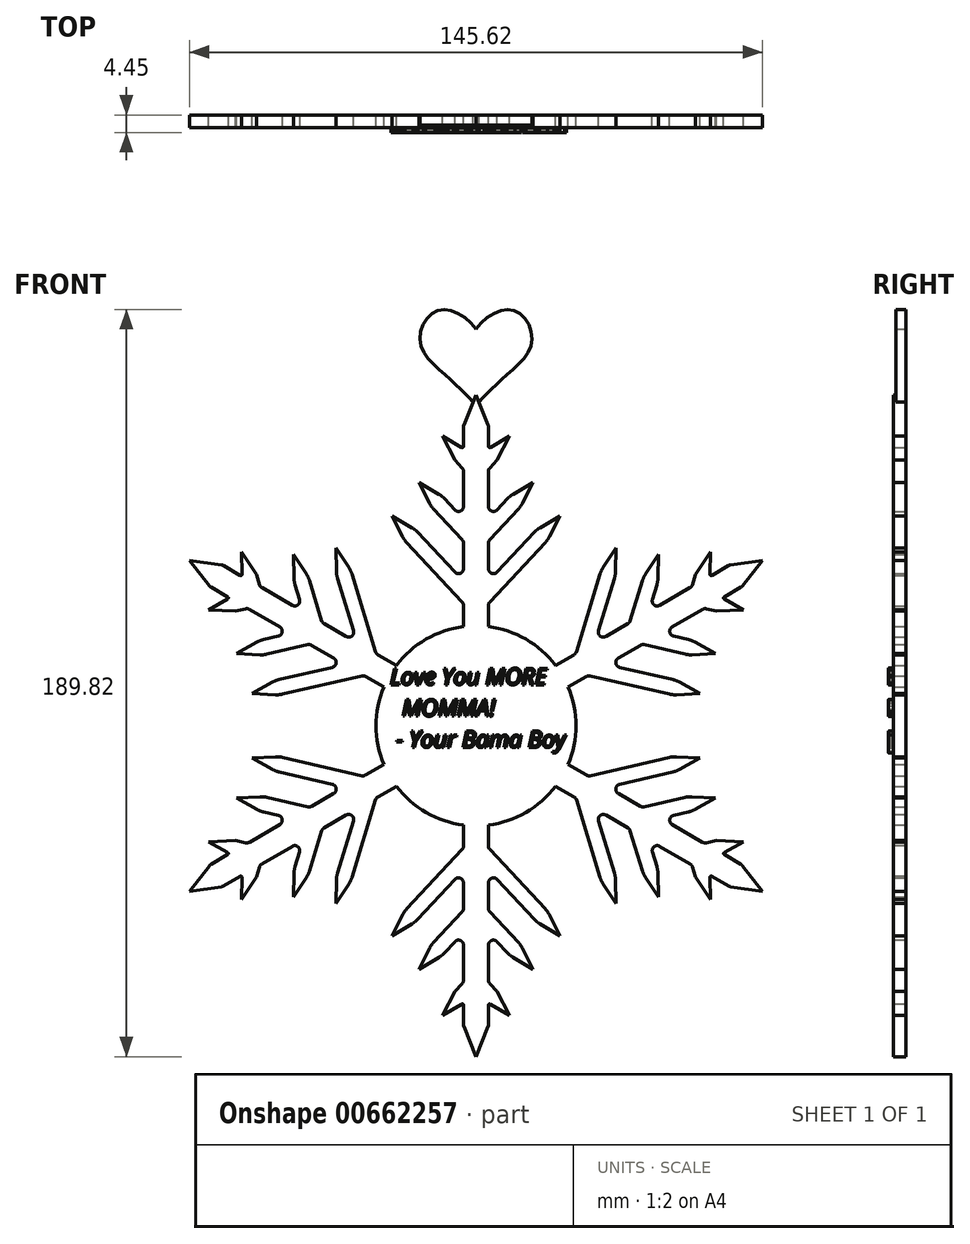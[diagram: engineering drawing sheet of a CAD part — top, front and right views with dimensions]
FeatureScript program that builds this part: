
annotation { "Feature Type Name" : "Feature", "Feature Type Description" : "" }
export const myFeature = defineFeature(function(context is Context, id is Id, definition is map)
    precondition{}
    {
        {
            var Q0;
            Q0=qCreatedBy(makeId("Front.planeOp"),FACE);
            var sketch = newSketch(context, id + "F0", { "sketchPlane" : qUnion([Q0])});
            skLineSegment(sketch, "E0", {"start": v(0, 76.2) * mm, "end": v(0, -76.2) * mm, "construction": true});
            skLineSegment(sketch, "E1", {"start": v(-76.2, 0) * mm, "end": v(76.2, 0) * mm, "construction": true});
            skPoint(sketch, "E2", {"position": v(0, 0) * mm});
            skArc(sketch, "E3", {"start": v(-23.41, 9.85) * mm, "mid": v(-25.4, 0) * mm, "end": v(-23.41, -9.85) * mm});
            skLineSegment(sketch, "E4.left", {"start": v(-3.17, 75.95) * mm, "end": v(-3.17, 71) * mm});
            skLineSegment(sketch, "E4.right", {"start": v(3.17, 75.95) * mm, "end": v(3.17, 71) * mm});
            skLineSegment(sketch, "E5", {"start": v(-3.17, 33.88) * mm, "end": v(-21.33, 53.35) * mm});
            skLineSegment(sketch, "E6", {"start": v(-3.17, 49.7) * mm, "end": v(-14.52, 61.87) * mm});
            skLineSegment(sketch, "E7", {"start": v(-3.17, 67.95) * mm, "end": v(-8.46, 73.61) * mm});
            skLineSegment(sketch, "E8", {"start": v(-3.52, 31.46) * mm, "end": v(-17.62, 46.58) * mm});
            skLineSegment(sketch, "E9", {"start": v(-14.83, 49.18) * mm, "end": v(-5.37, 39.03) * mm});
            skLineSegment(sketch, "E10", {"start": v(-3.52, 47.28) * mm, "end": v(-10.8, 55.1) * mm});
            skLineSegment(sketch, "E11", {"start": v(-8.02, 57.7) * mm, "end": v(-5.37, 54.85) * mm});
            skLineSegment(sketch, "E12", {"start": v(-3.52, 65.52) * mm, "end": v(-5.36, 67.5) * mm});
            skLineSegment(sketch, "E13", {"start": v(-18.64, 48.04) * mm, "end": v(-21.33, 53.35) * mm});
            skLineSegment(sketch, "E14", {"start": v(-16.22, 50.3) * mm, "end": v(-21.33, 53.35) * mm});
            skLineSegment(sketch, "E15", {"start": v(-3.64, 70.73) * mm, "end": v(-8.46, 73.61) * mm});
            skLineSegment(sketch, "E16", {"start": v(-5.36, 67.5) * mm, "end": v(-8.46, 73.61) * mm});
            skLineSegment(sketch, "E17", {"start": v(-11.83, 56.56) * mm, "end": v(-14.52, 61.87) * mm});
            skLineSegment(sketch, "E18", {"start": v(-9.4, 58.81) * mm, "end": v(-14.52, 61.87) * mm});
            skPoint(sketch, "E19.orphan", {"position": v(-7.07, 74.91) * mm});
            skPoint(sketch, "E20.orphan", {"position": v(-9.85, 72.31) * mm});
            skPoint(sketch, "E21.orphan", {"position": v(-13.12, 63.17) * mm});
            skPoint(sketch, "E22.orphan", {"position": v(-15.91, 60.57) * mm});
            skPoint(sketch, "E23.orphan", {"position": v(-19.94, 54.65) * mm});
            skPoint(sketch, "E24.orphan", {"position": v(-22.72, 52.05) * mm});
            skPoint(sketch, "E25.visualSharp", {"position": v(-15.45, 49.84) * mm});
            skArc(sketch, "E25.filletArc", {"start": v(-14.83, 49.18) * mm, "mid": v(-15.49, 49.79) * mm, "end": v(-16.22, 50.3) * mm});
            skPoint(sketch, "E26.visualSharp", {"position": v(-18.23, 47.24) * mm});
            skArc(sketch, "E26.filletArc", {"start": v(-18.64, 48.04) * mm, "mid": v(-18.18, 47.28) * mm, "end": v(-17.62, 46.58) * mm});
            skPoint(sketch, "E27.visualSharp", {"position": v(-11.42, 55.75) * mm});
            skArc(sketch, "E27.filletArc", {"start": v(-11.83, 56.56) * mm, "mid": v(-11.37, 55.79) * mm, "end": v(-10.8, 55.1) * mm});
            skPoint(sketch, "E28.visualSharp", {"position": v(-8.63, 58.35) * mm});
            skArc(sketch, "E28.filletArc", {"start": v(-8.02, 57.7) * mm, "mid": v(-8.67, 58.3) * mm, "end": v(-9.4, 58.81) * mm});
            skLineSegment(sketch, "E29.trimOffspring", {"start": v(-3.17, 30.59) * mm, "end": v(-3.17, 25.2) * mm});
            skLineSegment(sketch, "E30.trimOffspring", {"start": v(-3.17, 46.41) * mm, "end": v(-3.17, 39.9) * mm});
            skLineSegment(sketch, "E31.trimOffspring", {"start": v(-3.17, 64.65) * mm, "end": v(-3.17, 55.72) * mm});
            skPoint(sketch, "E32.visualSharp", {"position": v(-3.17, 70.46) * mm});
            skArc(sketch, "E32.filletArc", {"start": v(-3.64, 70.73) * mm, "mid": v(-3.33, 70.73) * mm, "end": v(-3.17, 71) * mm});
            skPoint(sketch, "E33.visualSharp", {"position": v(-3.17, 65.15) * mm});
            skArc(sketch, "E33.filletArc", {"start": v(-3.18, 64.65) * mm, "mid": v(-3.26, 65.12) * mm, "end": v(-3.52, 65.52) * mm});
            skPoint(sketch, "E34.visualSharp", {"position": v(-3.17, 52.5) * mm});
            skArc(sketch, "E34.filletArc", {"start": v(-5.37, 54.85) * mm, "mid": v(-3.98, 54.54) * mm, "end": v(-3.17, 55.72) * mm});
            skPoint(sketch, "E35.visualSharp", {"position": v(-3.17, 46.91) * mm});
            skArc(sketch, "E35.filletArc", {"start": v(-3.17, 46.41) * mm, "mid": v(-3.26, 46.88) * mm, "end": v(-3.52, 47.28) * mm});
            skPoint(sketch, "E36.visualSharp", {"position": v(-3.17, 36.68) * mm});
            skArc(sketch, "E36.filletArc", {"start": v(-5.37, 39.03) * mm, "mid": v(-3.98, 38.72) * mm, "end": v(-3.17, 39.9) * mm});
            skPoint(sketch, "E37.visualSharp", {"position": v(-3.17, 31.09) * mm});
            skArc(sketch, "E37.filletArc", {"start": v(-3.17, 30.59) * mm, "mid": v(-3.26, 31.05) * mm, "end": v(-3.52, 31.46) * mm});
            skLineSegment(sketch, "E38", {"start": v(-3.08, 76.43) * mm, "end": v(0, 84.07) * mm});
            skLineSegment(sketch, "E39", {"start": v(0, 84.07) * mm, "end": v(3.08, 76.43) * mm});
            skPoint(sketch, "E40.visualSharp", {"position": v(-3.17, 76.2) * mm});
            skArc(sketch, "E40.filletArc", {"start": v(-3.08, 76.43) * mm, "mid": v(-3.15, 76.2) * mm, "end": v(-3.17, 75.95) * mm});
            skPoint(sketch, "E41.visualSharp", {"position": v(3.18, 76.2) * mm});
            skArc(sketch, "E41.filletArc", {"start": v(3.17, 75.95) * mm, "mid": v(3.15, 76.2) * mm, "end": v(3.08, 76.43) * mm});
            skArc(sketch, "E42.MirrorCS", {"start": v(3.08, 76.43) * mm, "mid": v(3.15, 76.2) * mm, "end": v(3.17, 75.95) * mm});
            skArc(sketch, "E43.MirrorCS", {"start": v(3.64, 70.73) * mm, "mid": v(3.33, 70.73) * mm, "end": v(3.17, 71) * mm});
            skArc(sketch, "E44.MirrorCS", {"start": v(11.83, 56.56) * mm, "mid": v(11.37, 55.79) * mm, "end": v(10.8, 55.1) * mm});
            skArc(sketch, "E45.MirrorCS", {"start": v(3.17, 30.59) * mm, "mid": v(3.26, 31.05) * mm, "end": v(3.52, 31.46) * mm});
            skArc(sketch, "E46.MirrorCS", {"start": v(3.18, 64.65) * mm, "mid": v(3.26, 65.12) * mm, "end": v(3.52, 65.52) * mm});
            skArc(sketch, "E47.MirrorCS", {"start": v(3.17, 46.41) * mm, "mid": v(3.26, 46.88) * mm, "end": v(3.52, 47.28) * mm});
            skArc(sketch, "E48.MirrorCS", {"start": v(18.64, 48.04) * mm, "mid": v(18.18, 47.28) * mm, "end": v(17.62, 46.58) * mm});
            skArc(sketch, "E49.MirrorCS", {"start": v(8.02, 57.7) * mm, "mid": v(8.67, 58.3) * mm, "end": v(9.4, 58.81) * mm});
            skArc(sketch, "E50.MirrorCS", {"start": v(14.83, 49.18) * mm, "mid": v(15.49, 49.79) * mm, "end": v(16.22, 50.3) * mm});
            skArc(sketch, "E51.MirrorCS", {"start": v(5.37, 39.03) * mm, "mid": v(3.98, 38.72) * mm, "end": v(3.17, 39.9) * mm});
            skLineSegment(sketch, "E52.MirrorCS", {"start": v(3.52, 65.52) * mm, "end": v(5.36, 67.5) * mm});
            skArc(sketch, "E53.MirrorCS", {"start": v(5.37, 54.85) * mm, "mid": v(3.98, 54.54) * mm, "end": v(3.17, 55.72) * mm});
            skPoint(sketch, "E54.MirrorP", {"position": v(3.17, 65.15) * mm});
            skPoint(sketch, "E55.MirrorP", {"position": v(7.07, 74.91) * mm});
            skLineSegment(sketch, "E56.MirrorCS", {"start": v(11.83, 56.56) * mm, "end": v(14.52, 61.87) * mm});
            skLineSegment(sketch, "E57.MirrorCS", {"start": v(18.64, 48.04) * mm, "end": v(21.33, 53.35) * mm});
            skLineSegment(sketch, "E58.MirrorCS", {"start": v(3.17, 46.41) * mm, "end": v(3.17, 39.9) * mm});
            skPoint(sketch, "E59.MirrorP", {"position": v(3.17, 31.09) * mm});
            skPoint(sketch, "E60.MirrorP", {"position": v(18.23, 47.24) * mm});
            skLineSegment(sketch, "E61.MirrorCS", {"start": v(9.4, 58.81) * mm, "end": v(14.52, 61.87) * mm});
            skLineSegment(sketch, "E62.MirrorCS", {"start": v(16.22, 50.3) * mm, "end": v(21.33, 53.35) * mm});
            skPoint(sketch, "E63.MirrorP", {"position": v(22.72, 52.05) * mm});
            skPoint(sketch, "E64.MirrorP", {"position": v(8.63, 58.35) * mm});
            skPoint(sketch, "E65.MirrorP", {"position": v(3.17, 70.46) * mm});
            skPoint(sketch, "E66.MirrorP", {"position": v(3.17, 76.2) * mm});
            skPoint(sketch, "E67.MirrorP", {"position": v(15.91, 60.57) * mm});
            skPoint(sketch, "E68.MirrorP", {"position": v(9.85, 72.31) * mm});
            skLineSegment(sketch, "E69.MirrorCS", {"start": v(3.17, 33.88) * mm, "end": v(21.33, 53.35) * mm});
            skPoint(sketch, "E70.MirrorP", {"position": v(3.17, 52.5) * mm});
            skPoint(sketch, "E71.MirrorP", {"position": v(19.94, 54.65) * mm});
            skLineSegment(sketch, "E72.MirrorCS", {"start": v(3.17, 49.7) * mm, "end": v(14.52, 61.87) * mm});
            skLineSegment(sketch, "E73.MirrorCS", {"start": v(3.17, 67.95) * mm, "end": v(8.46, 73.61) * mm});
            skLineSegment(sketch, "E74.MirrorCS", {"start": v(3.52, 31.46) * mm, "end": v(17.62, 46.58) * mm});
            skPoint(sketch, "E75.MirrorP", {"position": v(11.42, 55.75) * mm});
            skLineSegment(sketch, "E76.MirrorCS", {"start": v(14.83, 49.18) * mm, "end": v(5.37, 39.03) * mm});
            skLineSegment(sketch, "E77.MirrorCS", {"start": v(3.52, 47.28) * mm, "end": v(10.8, 55.1) * mm});
            skPoint(sketch, "E78.MirrorP", {"position": v(13.12, 63.17) * mm});
            skLineSegment(sketch, "E79.MirrorCS", {"start": v(3.17, 64.65) * mm, "end": v(3.17, 55.72) * mm});
            skLineSegment(sketch, "E80.MirrorCS", {"start": v(5.36, 67.5) * mm, "end": v(8.46, 73.61) * mm});
            skLineSegment(sketch, "E81.MirrorCS", {"start": v(3.64, 70.73) * mm, "end": v(8.46, 73.61) * mm});
            skLineSegment(sketch, "E82.MirrorCS", {"start": v(8.02, 57.7) * mm, "end": v(5.37, 54.85) * mm});
            skPoint(sketch, "E83.MirrorP", {"position": v(3.17, 36.68) * mm});
            skPoint(sketch, "E84.MirrorP", {"position": v(15.45, 49.84) * mm});
            skPoint(sketch, "E85.MirrorP", {"position": v(3.17, 46.91) * mm});
            skLineSegment(sketch, "E86.trimOffspring", {"start": v(3.18, 31.09) * mm, "end": v(3.18, 25.2) * mm});
            skLineSegment(sketch, "E87.trimOffspring", {"start": v(3.18, 46.91) * mm, "end": v(3.18, 39.9) * mm});
            skLineSegment(sketch, "E88.trimOffspring", {"start": v(3.17, 65.15) * mm, "end": v(3.17, 55.72) * mm});
            skPoint(sketch, "E89.1.0", {"position": v(-35.44, 38.3) * mm});
            skPoint(sketch, "E89.1.1", {"position": v(-61.34, 43.58) * mm});
            skPoint(sketch, "E89.1.2", {"position": v(-28.51, 12.8) * mm});
            skPoint(sketch, "E89.1.3", {"position": v(-68.4, 31.34) * mm});
            skLineSegment(sketch, "E89.1.4", {"start": v(-67.73, 35.54) * mm, "end": v(-72.8, 42.04) * mm});
            skLineSegment(sketch, "E89.1.5", {"start": v(-72.8, 42.04) * mm, "end": v(-64.65, 40.88) * mm});
            skLineSegment(sketch, "E89.1.6", {"start": v(-27.76, 19.7) * mm, "end": v(-35.54, 45.15) * mm});
            skPoint(sketch, "E89.1.7", {"position": v(-39.04, 26.2) * mm});
            skPoint(sketch, "E89.1.8", {"position": v(-59.43, 37.98) * mm});
            skPoint(sketch, "E89.1.9", {"position": v(-54, 17.99) * mm});
            skPoint(sketch, "E89.1.10", {"position": v(-67.55, 27.62) * mm});
            skPoint(sketch, "E89.1.11", {"position": v(-54.84, 35.33) * mm});
            skLineSegment(sketch, "E89.1.12", {"start": v(-29, 12.68) * mm, "end": v(-49.15, 8.03) * mm});
            skPoint(sketch, "E89.1.13", {"position": v(-44.5, 44.06) * mm});
            skPoint(sketch, "E89.1.14", {"position": v(-46.22, 36.65) * mm});
            skPoint(sketch, "E89.1.15", {"position": v(-30.18, 21.09) * mm});
            skLineSegment(sketch, "E89.1.16", {"start": v(-25.48, 18.77) * mm, "end": v(-31.53, 38.55) * mm});
            skPoint(sketch, "E89.1.17", {"position": v(-37.36, 44.6) * mm});
            skPoint(sketch, "E89.1.18", {"position": v(-57.3, 10.06) * mm});
            skPoint(sketch, "E89.1.19", {"position": v(-42.21, 20.7) * mm});
            skPoint(sketch, "E89.1.20", {"position": v(-25.34, 18.3) * mm});
            skLineSegment(sketch, "E89.1.21", {"start": v(-39.18, 26.68) * mm, "end": v(-42.3, 36.9) * mm});
            skPoint(sketch, "E89.1.22", {"position": v(-33.72, 45.7) * mm});
            skPoint(sketch, "E89.1.23", {"position": v(-48.14, 42.95) * mm});
            skPoint(sketch, "E89.1.24", {"position": v(-43.88, 29) * mm});
            skPoint(sketch, "E89.1.25", {"position": v(-60.4, 16.5) * mm});
            skLineSegment(sketch, "E89.1.26", {"start": v(-54.4, 35.08) * mm, "end": v(-46.67, 30.61) * mm});
            skPoint(sketch, "E89.1.27", {"position": v(-56.44, 6.35) * mm});
            skLineSegment(sketch, "E89.1.28", {"start": v(-35.17, 37.44) * mm, "end": v(-31.12, 24.17) * mm});
            skPoint(sketch, "E89.1.29", {"position": v(-42.57, 37.77) * mm});
            skPoint(sketch, "E89.1.30", {"position": v(-31.8, 39.41) * mm});
            skPoint(sketch, "E89.1.31", {"position": v(-57.7, 44.7) * mm});
            skLineSegment(sketch, "E89.1.32", {"start": v(-50, 11.74) * mm, "end": v(-36.5, 14.86) * mm});
            skLineSegment(sketch, "E89.1.33", {"start": v(-30.93, 14.2) * mm, "end": v(-56.87, 8.2) * mm});
            skPoint(sketch, "E89.1.34", {"position": v(-58.01, 29.83) * mm});
            skLineSegment(sketch, "E89.1.35", {"start": v(-42.7, 20.6) * mm, "end": v(-53.12, 18.19) * mm});
            skPoint(sketch, "E89.1.36", {"position": v(-67.58, 35.35) * mm});
            skPoint(sketch, "E89.1.37", {"position": v(-50.03, 7.83) * mm});
            skPoint(sketch, "E89.1.38", {"position": v(-62.6, 32.48) * mm});
            skLineSegment(sketch, "E89.1.39", {"start": v(-57.58, 29.58) * mm, "end": v(-49.84, 25.11) * mm});
            skPoint(sketch, "E89.1.40", {"position": v(-50.88, 11.54) * mm});
            skPoint(sketch, "E89.1.41", {"position": v(-33.35, 15.59) * mm});
            skPoint(sketch, "E89.1.42", {"position": v(-54.85, 21.7) * mm});
            skPoint(sketch, "E89.1.43", {"position": v(-64.4, 40.85) * mm});
            skPoint(sketch, "E89.1.44", {"position": v(-61.27, 20.22) * mm});
            skPoint(sketch, "E89.1.45", {"position": v(-47.05, 23.5) * mm});
            skLineSegment(sketch, "E89.1.46", {"start": v(-54.84, 35.33) * mm, "end": v(-46.67, 30.61) * mm});
            skLineSegment(sketch, "E89.1.47", {"start": v(-44.63, 22.1) * mm, "end": v(-60.84, 18.36) * mm});
            skLineSegment(sketch, "E89.1.48", {"start": v(-28.08, 12.55) * mm, "end": v(-23.41, 9.85) * mm});
            skPoint(sketch, "E89.1.49", {"position": v(-64.4, 40.85) * mm});
            skLineSegment(sketch, "E89.1.50", {"start": v(-25.34, 18.3) * mm, "end": v(-20.24, 15.35) * mm});
            skLineSegment(sketch, "E89.1.52", {"start": v(-41.46, 27.6) * mm, "end": v(-46.32, 43.5) * mm});
            skLineSegment(sketch, "E89.1.53", {"start": v(-55.77, 38.4) * mm, "end": v(-59.52, 44.13) * mm});
            skLineSegment(sketch, "E89.1.54", {"start": v(-39.04, 26.2) * mm, "end": v(-32.97, 22.7) * mm});
            skArc(sketch, "E89.1.55", {"start": v(-43.07, 38.52) * mm, "mid": v(-42.63, 37.74) * mm, "end": v(-42.3, 36.9) * mm});
            skLineSegment(sketch, "E89.1.56", {"start": v(-41.78, 20.46) * mm, "end": v(-36.14, 17.2) * mm});
            skLineSegment(sketch, "E89.1.57", {"start": v(-43.07, 38.52) * mm, "end": v(-46.32, 43.5) * mm});
            skLineSegment(sketch, "E89.1.58", {"start": v(-61.14, 29.1) * mm, "end": v(-67.98, 29.48) * mm});
            skLineSegment(sketch, "E89.1.59", {"start": v(-54.9, 18.03) * mm, "end": v(-60.84, 18.36) * mm});
            skLineSegment(sketch, "E89.1.60", {"start": v(-32.29, 40.16) * mm, "end": v(-35.54, 45.15) * mm});
            skArc(sketch, "E89.1.61", {"start": v(-44.82, 32.08) * mm, "mid": v(-45.24, 30.72) * mm, "end": v(-46.67, 30.61) * mm});
            skLineSegment(sketch, "E89.1.62", {"start": v(-45.95, 35.8) * mm, "end": v(-44.82, 32.08) * mm});
            skArc(sketch, "E89.1.63", {"start": v(-36.5, 14.86) * mm, "mid": v(-35.52, 15.91) * mm, "end": v(-36.14, 17.2) * mm});
            skLineSegment(sketch, "E89.1.64", {"start": v(-35.45, 39.2) * mm, "end": v(-35.54, 45.15) * mm});
            skArc(sketch, "E89.1.65", {"start": v(-45.95, 35.8) * mm, "mid": v(-46.15, 36.66) * mm, "end": v(-46.23, 37.55) * mm});
            skArc(sketch, "E89.1.66", {"start": v(-50.2, 22.77) * mm, "mid": v(-49.22, 23.82) * mm, "end": v(-49.84, 25.11) * mm});
            skArc(sketch, "E89.1.67", {"start": v(-35.17, 37.44) * mm, "mid": v(-35.37, 38.3) * mm, "end": v(-35.45, 39.2) * mm});
            skLineSegment(sketch, "E89.1.68", {"start": v(-46.23, 37.55) * mm, "end": v(-46.32, 43.5) * mm});
            skArc(sketch, "E89.1.69", {"start": v(-32.29, 40.16) * mm, "mid": v(-31.85, 39.38) * mm, "end": v(-31.53, 38.55) * mm});
            skArc(sketch, "E89.1.70", {"start": v(-53.97, 21.9) * mm, "mid": v(-54.83, 21.64) * mm, "end": v(-55.64, 21.26) * mm});
            skLineSegment(sketch, "E89.1.71", {"start": v(-63.07, 32.22) * mm, "end": v(-67.98, 29.48) * mm});
            skLineSegment(sketch, "E89.1.72", {"start": v(-60.43, 31.22) * mm, "end": v(-67.98, 29.48) * mm});
            skLineSegment(sketch, "E89.1.73", {"start": v(-50.93, 7.88) * mm, "end": v(-56.87, 8.2) * mm});
            skLineSegment(sketch, "E89.1.74", {"start": v(-57.26, 36.72) * mm, "end": v(-59.52, 44.13) * mm});
            skArc(sketch, "E89.1.75", {"start": v(-24.9, 18.04) * mm, "mid": v(-25.26, 18.35) * mm, "end": v(-25.48, 18.77) * mm});
            skLineSegment(sketch, "E89.1.76", {"start": v(-53.97, 21.9) * mm, "end": v(-50.2, 22.77) * mm});
            skLineSegment(sketch, "E89.1.77", {"start": v(-51.67, 11.1) * mm, "end": v(-56.87, 8.2) * mm});
            skArc(sketch, "E89.1.78", {"start": v(-28.08, 12.55) * mm, "mid": v(-28.53, 12.7) * mm, "end": v(-29, 12.68) * mm});
            skLineSegment(sketch, "E89.1.79", {"start": v(-59.44, 38.51) * mm, "end": v(-59.52, 44.13) * mm});
            skArc(sketch, "E89.1.80", {"start": v(-54.9, 18.03) * mm, "mid": v(-54, 18.05) * mm, "end": v(-53.12, 18.19) * mm});
            skArc(sketch, "E89.1.81", {"start": v(-38.6, 25.95) * mm, "mid": v(-38.96, 26.26) * mm, "end": v(-39.18, 26.68) * mm});
            skArc(sketch, "E89.1.82", {"start": v(-41.78, 20.46) * mm, "mid": v(-42.23, 20.61) * mm, "end": v(-42.7, 20.6) * mm});
            skArc(sketch, "E89.1.83", {"start": v(-31.12, 24.17) * mm, "mid": v(-31.54, 22.8) * mm, "end": v(-32.97, 22.7) * mm});
            skArc(sketch, "E89.1.84", {"start": v(-50.93, 7.88) * mm, "mid": v(-50.03, 7.9) * mm, "end": v(-49.15, 8.03) * mm});
            skArc(sketch, "E89.1.85", {"start": v(-57.58, 29.58) * mm, "mid": v(-58.03, 29.73) * mm, "end": v(-58.5, 29.71) * mm});
            skArc(sketch, "E89.1.86", {"start": v(-50, 11.74) * mm, "mid": v(-50.86, 11.48) * mm, "end": v(-51.67, 11.1) * mm});
            skLineSegment(sketch, "E89.1.87", {"start": v(-38.6, 25.95) * mm, "end": v(-32.97, 22.7) * mm});
            skLineSegment(sketch, "E89.1.88", {"start": v(-55.64, 21.26) * mm, "end": v(-60.84, 18.36) * mm});
            skArc(sketch, "E89.1.89", {"start": v(-54.4, 35.08) * mm, "mid": v(-54.76, 35.39) * mm, "end": v(-54.98, 35.8) * mm});
            skLineSegment(sketch, "E89.1.90", {"start": v(-58.5, 29.71) * mm, "end": v(-61.14, 29.1) * mm});
            skLineSegment(sketch, "E89.1.91", {"start": v(-54.98, 35.8) * mm, "end": v(-55.77, 38.4) * mm});
            skLineSegment(sketch, "E89.1.92", {"start": v(-67.37, 35.23) * mm, "end": v(-63.07, 32.75) * mm});
            skLineSegment(sketch, "E89.1.93", {"start": v(-64.2, 40.73) * mm, "end": v(-59.9, 38.25) * mm});
            skArc(sketch, "E89.1.94", {"start": v(-64.2, 40.73) * mm, "mid": v(-64.41, 40.83) * mm, "end": v(-64.65, 40.88) * mm});
            skArc(sketch, "E89.1.95", {"start": v(-63.07, 32.22) * mm, "mid": v(-62.92, 32.48) * mm, "end": v(-63.07, 32.75) * mm});
            skArc(sketch, "E89.1.96", {"start": v(-67.73, 35.54) * mm, "mid": v(-67.56, 35.37) * mm, "end": v(-67.37, 35.23) * mm});
            skArc(sketch, "E89.1.97", {"start": v(-59.44, 38.51) * mm, "mid": v(-59.59, 38.25) * mm, "end": v(-59.9, 38.25) * mm});
            skLineSegment(sketch, "E89.1.98", {"start": v(-64.2, 40.73) * mm, "end": v(-59.9, 38.25) * mm});
            skArc(sketch, "E89.1.99", {"start": v(-64.65, 40.88) * mm, "mid": v(-64.41, 40.83) * mm, "end": v(-64.2, 40.73) * mm});
            skPoint(sketch, "E89.2.0", {"position": v(-50.88, -11.54) * mm});
            skPoint(sketch, "E89.2.1", {"position": v(-68.4, -31.34) * mm});
            skPoint(sketch, "E89.2.2", {"position": v(-25.34, -18.3) * mm});
            skPoint(sketch, "E89.2.3", {"position": v(-61.34, -43.58) * mm});
            skLineSegment(sketch, "E89.2.4", {"start": v(-64.65, -40.88) * mm, "end": v(-72.8, -42.04) * mm});
            skLineSegment(sketch, "E89.2.5", {"start": v(-72.8, -42.04) * mm, "end": v(-67.73, -35.54) * mm});
            skLineSegment(sketch, "E89.2.6", {"start": v(-30.93, -14.2) * mm, "end": v(-56.87, -8.2) * mm});
            skPoint(sketch, "E89.2.7", {"position": v(-42.21, -20.7) * mm});
            skPoint(sketch, "E89.2.8", {"position": v(-62.6, -32.48) * mm});
            skPoint(sketch, "E89.2.9", {"position": v(-42.57, -37.77) * mm});
            skPoint(sketch, "E89.2.10", {"position": v(-57.7, -44.7) * mm});
            skPoint(sketch, "E89.2.11", {"position": v(-58.01, -29.83) * mm});
            skLineSegment(sketch, "E89.2.12", {"start": v(-25.48, -18.77) * mm, "end": v(-31.53, -38.55) * mm});
            skPoint(sketch, "E89.2.13", {"position": v(-60.4, -16.5) * mm});
            skPoint(sketch, "E89.2.14", {"position": v(-54.85, -21.7) * mm});
            skPoint(sketch, "E89.2.15", {"position": v(-33.35, -15.59) * mm});
            skLineSegment(sketch, "E89.2.16", {"start": v(-29, -12.68) * mm, "end": v(-49.15, -8.03) * mm});
            skPoint(sketch, "E89.2.17", {"position": v(-57.3, -10.06) * mm});
            skPoint(sketch, "E89.2.18", {"position": v(-37.36, -44.6) * mm});
            skPoint(sketch, "E89.2.19", {"position": v(-39.04, -26.2) * mm});
            skPoint(sketch, "E89.2.20", {"position": v(-28.51, -12.8) * mm});
            skLineSegment(sketch, "E89.2.21", {"start": v(-42.7, -20.6) * mm, "end": v(-53.12, -18.19) * mm});
            skPoint(sketch, "E89.2.22", {"position": v(-56.44, -6.35) * mm});
            skPoint(sketch, "E89.2.23", {"position": v(-61.27, -20.22) * mm});
            skPoint(sketch, "E89.2.24", {"position": v(-47.05, -23.5) * mm});
            skPoint(sketch, "E89.2.25", {"position": v(-44.5, -44.06) * mm});
            skLineSegment(sketch, "E89.2.26", {"start": v(-57.58, -29.58) * mm, "end": v(-49.84, -25.11) * mm});
            skPoint(sketch, "E89.2.27", {"position": v(-33.72, -45.7) * mm});
            skLineSegment(sketch, "E89.2.28", {"start": v(-50, -11.74) * mm, "end": v(-36.5, -14.86) * mm});
            skPoint(sketch, "E89.2.29", {"position": v(-54, -17.99) * mm});
            skPoint(sketch, "E89.2.30", {"position": v(-50.03, -7.83) * mm});
            skPoint(sketch, "E89.2.31", {"position": v(-67.55, -27.62) * mm});
            skLineSegment(sketch, "E89.2.32", {"start": v(-35.17, -37.44) * mm, "end": v(-31.12, -24.17) * mm});
            skLineSegment(sketch, "E89.2.33", {"start": v(-27.76, -19.7) * mm, "end": v(-35.54, -45.15) * mm});
            skPoint(sketch, "E89.2.34", {"position": v(-54.84, -35.33) * mm});
            skLineSegment(sketch, "E89.2.35", {"start": v(-39.18, -26.68) * mm, "end": v(-42.3, -36.9) * mm});
            skPoint(sketch, "E89.2.36", {"position": v(-64.4, -40.85) * mm});
            skPoint(sketch, "E89.2.37", {"position": v(-31.8, -39.41) * mm});
            skPoint(sketch, "E89.2.38", {"position": v(-59.43, -37.98) * mm});
            skLineSegment(sketch, "E89.2.39", {"start": v(-54.4, -35.08) * mm, "end": v(-46.67, -30.61) * mm});
            skPoint(sketch, "E89.2.40", {"position": v(-35.44, -38.3) * mm});
            skPoint(sketch, "E89.2.41", {"position": v(-30.18, -21.09) * mm});
            skPoint(sketch, "E89.2.42", {"position": v(-46.22, -36.65) * mm});
            skPoint(sketch, "E89.2.43", {"position": v(-67.58, -35.35) * mm});
            skPoint(sketch, "E89.2.44", {"position": v(-48.14, -42.95) * mm});
            skPoint(sketch, "E89.2.45", {"position": v(-43.88, -29) * mm});
            skLineSegment(sketch, "E89.2.46", {"start": v(-58.01, -29.83) * mm, "end": v(-49.84, -25.11) * mm});
            skLineSegment(sketch, "E89.2.47", {"start": v(-41.46, -27.6) * mm, "end": v(-46.32, -43.5) * mm});
            skLineSegment(sketch, "E89.2.48", {"start": v(-24.9, -18.04) * mm, "end": v(-20.24, -15.35) * mm});
            skPoint(sketch, "E89.2.49", {"position": v(-67.58, -35.35) * mm});
            skLineSegment(sketch, "E89.2.50", {"start": v(-28.51, -12.8) * mm, "end": v(-23.41, -9.85) * mm});
            skLineSegment(sketch, "E89.2.52", {"start": v(-44.63, -22.1) * mm, "end": v(-60.84, -18.36) * mm});
            skLineSegment(sketch, "E89.2.53", {"start": v(-61.14, -29.1) * mm, "end": v(-67.98, -29.48) * mm});
            skLineSegment(sketch, "E89.2.54", {"start": v(-42.21, -20.7) * mm, "end": v(-36.14, -17.2) * mm});
            skArc(sketch, "E89.2.55", {"start": v(-54.9, -18.03) * mm, "mid": v(-54, -18.05) * mm, "end": v(-53.12, -18.19) * mm});
            skLineSegment(sketch, "E89.2.56", {"start": v(-38.6, -25.95) * mm, "end": v(-32.97, -22.7) * mm});
            skLineSegment(sketch, "E89.2.57", {"start": v(-54.9, -18.03) * mm, "end": v(-60.84, -18.36) * mm});
            skLineSegment(sketch, "E89.2.58", {"start": v(-55.77, -38.4) * mm, "end": v(-59.52, -44.13) * mm});
            skLineSegment(sketch, "E89.2.59", {"start": v(-43.07, -38.52) * mm, "end": v(-46.32, -43.5) * mm});
            skLineSegment(sketch, "E89.2.60", {"start": v(-50.93, -7.88) * mm, "end": v(-56.87, -8.2) * mm});
            skArc(sketch, "E89.2.61", {"start": v(-50.2, -22.77) * mm, "mid": v(-49.22, -23.82) * mm, "end": v(-49.84, -25.11) * mm});
            skLineSegment(sketch, "E89.2.62", {"start": v(-53.97, -21.9) * mm, "end": v(-50.2, -22.77) * mm});
            skArc(sketch, "E89.2.63", {"start": v(-31.12, -24.17) * mm, "mid": v(-31.54, -22.8) * mm, "end": v(-32.97, -22.7) * mm});
            skLineSegment(sketch, "E89.2.64", {"start": v(-51.67, -11.1) * mm, "end": v(-56.87, -8.2) * mm});
            skArc(sketch, "E89.2.65", {"start": v(-53.97, -21.9) * mm, "mid": v(-54.83, -21.64) * mm, "end": v(-55.64, -21.26) * mm});
            skArc(sketch, "E89.2.66", {"start": v(-44.82, -32.08) * mm, "mid": v(-45.24, -30.72) * mm, "end": v(-46.67, -30.61) * mm});
            skArc(sketch, "E89.2.67", {"start": v(-50, -11.74) * mm, "mid": v(-50.86, -11.48) * mm, "end": v(-51.67, -11.1) * mm});
            skLineSegment(sketch, "E89.2.68", {"start": v(-55.64, -21.26) * mm, "end": v(-60.84, -18.36) * mm});
            skArc(sketch, "E89.2.69", {"start": v(-50.93, -7.88) * mm, "mid": v(-50.03, -7.9) * mm, "end": v(-49.15, -8.03) * mm});
            skArc(sketch, "E89.2.70", {"start": v(-45.95, -35.8) * mm, "mid": v(-46.15, -36.66) * mm, "end": v(-46.23, -37.55) * mm});
            skLineSegment(sketch, "E89.2.71", {"start": v(-59.44, -38.51) * mm, "end": v(-59.52, -44.13) * mm});
            skLineSegment(sketch, "E89.2.72", {"start": v(-57.26, -36.72) * mm, "end": v(-59.52, -44.13) * mm});
            skLineSegment(sketch, "E89.2.73", {"start": v(-32.29, -40.16) * mm, "end": v(-35.54, -45.15) * mm});
            skLineSegment(sketch, "E89.2.74", {"start": v(-60.43, -31.22) * mm, "end": v(-67.98, -29.48) * mm});
            skArc(sketch, "E89.2.75", {"start": v(-28.08, -12.55) * mm, "mid": v(-28.53, -12.7) * mm, "end": v(-29, -12.68) * mm});
            skLineSegment(sketch, "E89.2.76", {"start": v(-45.95, -35.8) * mm, "end": v(-44.82, -32.08) * mm});
            skLineSegment(sketch, "E89.2.77", {"start": v(-35.45, -39.2) * mm, "end": v(-35.54, -45.15) * mm});
            skArc(sketch, "E89.2.78", {"start": v(-24.9, -18.04) * mm, "mid": v(-25.26, -18.35) * mm, "end": v(-25.48, -18.77) * mm});
            skLineSegment(sketch, "E89.2.79", {"start": v(-63.07, -32.22) * mm, "end": v(-67.98, -29.48) * mm});
            skArc(sketch, "E89.2.80", {"start": v(-43.07, -38.52) * mm, "mid": v(-42.63, -37.74) * mm, "end": v(-42.3, -36.9) * mm});
            skArc(sketch, "E89.2.81", {"start": v(-41.78, -20.46) * mm, "mid": v(-42.23, -20.61) * mm, "end": v(-42.7, -20.6) * mm});
            skArc(sketch, "E89.2.82", {"start": v(-38.6, -25.95) * mm, "mid": v(-38.96, -26.26) * mm, "end": v(-39.18, -26.68) * mm});
            skArc(sketch, "E89.2.83", {"start": v(-36.5, -14.86) * mm, "mid": v(-35.52, -15.91) * mm, "end": v(-36.14, -17.2) * mm});
            skArc(sketch, "E89.2.84", {"start": v(-32.29, -40.16) * mm, "mid": v(-31.85, -39.38) * mm, "end": v(-31.53, -38.55) * mm});
            skArc(sketch, "E89.2.85", {"start": v(-54.4, -35.08) * mm, "mid": v(-54.76, -35.39) * mm, "end": v(-54.98, -35.8) * mm});
            skArc(sketch, "E89.2.86", {"start": v(-35.17, -37.44) * mm, "mid": v(-35.37, -38.3) * mm, "end": v(-35.45, -39.2) * mm});
            skLineSegment(sketch, "E89.2.87", {"start": v(-41.78, -20.46) * mm, "end": v(-36.14, -17.2) * mm});
            skLineSegment(sketch, "E89.2.88", {"start": v(-46.23, -37.55) * mm, "end": v(-46.32, -43.5) * mm});
            skArc(sketch, "E89.2.89", {"start": v(-57.58, -29.58) * mm, "mid": v(-58.03, -29.73) * mm, "end": v(-58.5, -29.71) * mm});
            skLineSegment(sketch, "E89.2.90", {"start": v(-54.98, -35.8) * mm, "end": v(-55.77, -38.4) * mm});
            skLineSegment(sketch, "E89.2.91", {"start": v(-58.5, -29.71) * mm, "end": v(-61.14, -29.1) * mm});
            skLineSegment(sketch, "E89.2.92", {"start": v(-64.2, -40.73) * mm, "end": v(-59.9, -38.25) * mm});
            skLineSegment(sketch, "E89.2.93", {"start": v(-67.37, -35.23) * mm, "end": v(-63.07, -32.75) * mm});
            skArc(sketch, "E89.2.94", {"start": v(-67.37, -35.23) * mm, "mid": v(-67.56, -35.37) * mm, "end": v(-67.73, -35.54) * mm});
            skArc(sketch, "E89.2.95", {"start": v(-59.44, -38.51) * mm, "mid": v(-59.59, -38.25) * mm, "end": v(-59.9, -38.25) * mm});
            skArc(sketch, "E89.2.96", {"start": v(-64.65, -40.88) * mm, "mid": v(-64.41, -40.83) * mm, "end": v(-64.2, -40.73) * mm});
            skArc(sketch, "E89.2.97", {"start": v(-63.07, -32.22) * mm, "mid": v(-62.92, -32.48) * mm, "end": v(-63.07, -32.75) * mm});
            skLineSegment(sketch, "E89.2.98", {"start": v(-67.37, -35.23) * mm, "end": v(-63.07, -32.75) * mm});
            skArc(sketch, "E89.2.99", {"start": v(-67.73, -35.54) * mm, "mid": v(-67.56, -35.37) * mm, "end": v(-67.37, -35.23) * mm});
            skPoint(sketch, "E89.3.0", {"position": v(-15.45, -49.84) * mm});
            skPoint(sketch, "E89.3.1", {"position": v(-7.07, -74.91) * mm});
            skPoint(sketch, "E89.3.2", {"position": v(3.17, -31.09) * mm});
            skPoint(sketch, "E89.3.3", {"position": v(7.07, -74.91) * mm});
            skLineSegment(sketch, "E89.3.4", {"start": v(3.08, -76.43) * mm, "end": v(0, -84.07) * mm});
            skLineSegment(sketch, "E89.3.5", {"start": v(0, -84.07) * mm, "end": v(-3.08, -76.43) * mm});
            skLineSegment(sketch, "E89.3.6", {"start": v(-3.17, -33.88) * mm, "end": v(-21.33, -53.35) * mm});
            skPoint(sketch, "E89.3.7", {"position": v(-3.18, -46.91) * mm});
            skPoint(sketch, "E89.3.8", {"position": v(-3.18, -70.46) * mm});
            skPoint(sketch, "E89.3.9", {"position": v(11.42, -55.75) * mm});
            skPoint(sketch, "E89.3.10", {"position": v(9.85, -72.31) * mm});
            skPoint(sketch, "E89.3.11", {"position": v(-3.18, -65.15) * mm});
            skLineSegment(sketch, "E89.3.12", {"start": v(3.52, -31.46) * mm, "end": v(17.62, -46.58) * mm});
            skPoint(sketch, "E89.3.13", {"position": v(-15.91, -60.57) * mm});
            skPoint(sketch, "E89.3.14", {"position": v(-8.63, -58.35) * mm});
            skPoint(sketch, "E89.3.15", {"position": v(-3.17, -36.68) * mm});
            skLineSegment(sketch, "E89.3.16", {"start": v(-3.52, -31.46) * mm, "end": v(-17.62, -46.58) * mm});
            skPoint(sketch, "E89.3.17", {"position": v(-19.94, -54.65) * mm});
            skPoint(sketch, "E89.3.18", {"position": v(19.94, -54.65) * mm});
            skPoint(sketch, "E89.3.19", {"position": v(3.17, -46.91) * mm});
            skPoint(sketch, "E89.3.20", {"position": v(-3.17, -31.09) * mm});
            skLineSegment(sketch, "E89.3.21", {"start": v(-3.52, -47.28) * mm, "end": v(-10.8, -55.1) * mm});
            skPoint(sketch, "E89.3.22", {"position": v(-22.72, -52.05) * mm});
            skPoint(sketch, "E89.3.23", {"position": v(-13.12, -63.17) * mm});
            skPoint(sketch, "E89.3.24", {"position": v(-3.18, -52.5) * mm});
            skPoint(sketch, "E89.3.25", {"position": v(15.91, -60.57) * mm});
            skLineSegment(sketch, "E89.3.26", {"start": v(-3.18, -64.65) * mm, "end": v(-3.18, -55.72) * mm});
            skPoint(sketch, "E89.3.27", {"position": v(22.72, -52.05) * mm});
            skLineSegment(sketch, "E89.3.28", {"start": v(-14.83, -49.18) * mm, "end": v(-5.37, -39.03) * mm});
            skPoint(sketch, "E89.3.29", {"position": v(-11.42, -55.75) * mm});
            skPoint(sketch, "E89.3.30", {"position": v(-18.23, -47.24) * mm});
            skPoint(sketch, "E89.3.31", {"position": v(-9.85, -72.31) * mm});
            skLineSegment(sketch, "E89.3.32", {"start": v(14.83, -49.18) * mm, "end": v(5.37, -39.03) * mm});
            skLineSegment(sketch, "E89.3.33", {"start": v(3.17, -33.88) * mm, "end": v(21.33, -53.35) * mm});
            skPoint(sketch, "E89.3.34", {"position": v(3.17, -65.15) * mm});
            skLineSegment(sketch, "E89.3.35", {"start": v(3.52, -47.28) * mm, "end": v(10.8, -55.1) * mm});
            skPoint(sketch, "E89.3.36", {"position": v(3.17, -76.2) * mm});
            skPoint(sketch, "E89.3.37", {"position": v(18.23, -47.24) * mm});
            skPoint(sketch, "E89.3.38", {"position": v(3.17, -70.46) * mm});
            skLineSegment(sketch, "E89.3.39", {"start": v(3.17, -64.65) * mm, "end": v(3.17, -55.72) * mm});
            skPoint(sketch, "E89.3.40", {"position": v(15.45, -49.84) * mm});
            skPoint(sketch, "E89.3.41", {"position": v(3.17, -36.68) * mm});
            skPoint(sketch, "E89.3.42", {"position": v(8.63, -58.35) * mm});
            skPoint(sketch, "E89.3.43", {"position": v(-3.18, -76.2) * mm});
            skPoint(sketch, "E89.3.44", {"position": v(13.12, -63.17) * mm});
            skPoint(sketch, "E89.3.45", {"position": v(3.17, -52.5) * mm});
            skLineSegment(sketch, "E89.3.46", {"start": v(-3.18, -65.15) * mm, "end": v(-3.18, -55.72) * mm});
            skLineSegment(sketch, "E89.3.47", {"start": v(3.17, -49.7) * mm, "end": v(14.52, -61.87) * mm});
            skLineSegment(sketch, "E89.3.48", {"start": v(3.17, -30.59) * mm, "end": v(3.17, -25.2) * mm});
            skPoint(sketch, "E89.3.49", {"position": v(-3.18, -76.2) * mm});
            skLineSegment(sketch, "E89.3.50", {"start": v(-3.18, -31.09) * mm, "end": v(-3.18, -25.2) * mm});
            skLineSegment(sketch, "E89.3.52", {"start": v(-3.18, -49.7) * mm, "end": v(-14.52, -61.87) * mm});
            skLineSegment(sketch, "E89.3.53", {"start": v(-5.36, -67.5) * mm, "end": v(-8.46, -73.61) * mm});
            skLineSegment(sketch, "E89.3.54", {"start": v(-3.18, -46.91) * mm, "end": v(-3.18, -39.9) * mm});
            skArc(sketch, "E89.3.55", {"start": v(-11.83, -56.56) * mm, "mid": v(-11.37, -55.79) * mm, "end": v(-10.8, -55.1) * mm});
            skLineSegment(sketch, "E89.3.56", {"start": v(3.17, -46.41) * mm, "end": v(3.17, -39.9) * mm});
            skLineSegment(sketch, "E89.3.57", {"start": v(-11.83, -56.56) * mm, "end": v(-14.52, -61.87) * mm});
            skLineSegment(sketch, "E89.3.58", {"start": v(5.36, -67.5) * mm, "end": v(8.46, -73.61) * mm});
            skLineSegment(sketch, "E89.3.59", {"start": v(11.83, -56.56) * mm, "end": v(14.52, -61.87) * mm});
            skLineSegment(sketch, "E89.3.60", {"start": v(-18.64, -48.04) * mm, "end": v(-21.33, -53.35) * mm});
            skArc(sketch, "E89.3.61", {"start": v(-5.37, -54.85) * mm, "mid": v(-3.98, -54.54) * mm, "end": v(-3.17, -55.72) * mm});
            skLineSegment(sketch, "E89.3.62", {"start": v(-8.02, -57.7) * mm, "end": v(-5.37, -54.85) * mm});
            skArc(sketch, "E89.3.63", {"start": v(5.37, -39.03) * mm, "mid": v(3.98, -38.72) * mm, "end": v(3.17, -39.9) * mm});
            skLineSegment(sketch, "E89.3.64", {"start": v(-16.22, -50.3) * mm, "end": v(-21.33, -53.35) * mm});
            skArc(sketch, "E89.3.65", {"start": v(-8.02, -57.7) * mm, "mid": v(-8.67, -58.3) * mm, "end": v(-9.4, -58.81) * mm});
            skArc(sketch, "E89.3.66", {"start": v(5.37, -54.85) * mm, "mid": v(3.98, -54.54) * mm, "end": v(3.17, -55.72) * mm});
            skArc(sketch, "E89.3.67", {"start": v(-14.83, -49.18) * mm, "mid": v(-15.49, -49.79) * mm, "end": v(-16.22, -50.3) * mm});
            skLineSegment(sketch, "E89.3.68", {"start": v(-9.4, -58.81) * mm, "end": v(-14.52, -61.87) * mm});
            skArc(sketch, "E89.3.69", {"start": v(-18.64, -48.04) * mm, "mid": v(-18.18, -47.28) * mm, "end": v(-17.62, -46.58) * mm});
            skArc(sketch, "E89.3.70", {"start": v(8.02, -57.7) * mm, "mid": v(8.67, -58.3) * mm, "end": v(9.4, -58.81) * mm});
            skLineSegment(sketch, "E89.3.71", {"start": v(3.64, -70.73) * mm, "end": v(8.46, -73.61) * mm});
            skLineSegment(sketch, "E89.3.72", {"start": v(3.17, -67.95) * mm, "end": v(8.46, -73.61) * mm});
            skLineSegment(sketch, "E89.3.73", {"start": v(18.64, -48.04) * mm, "end": v(21.33, -53.35) * mm});
            skLineSegment(sketch, "E89.3.74", {"start": v(-3.18, -67.95) * mm, "end": v(-8.46, -73.61) * mm});
            skArc(sketch, "E89.3.75", {"start": v(-3.17, -30.59) * mm, "mid": v(-3.26, -31.05) * mm, "end": v(-3.52, -31.46) * mm});
            skLineSegment(sketch, "E89.3.76", {"start": v(8.02, -57.7) * mm, "end": v(5.37, -54.85) * mm});
            skLineSegment(sketch, "E89.3.77", {"start": v(16.22, -50.3) * mm, "end": v(21.33, -53.35) * mm});
            skArc(sketch, "E89.3.78", {"start": v(3.17, -30.59) * mm, "mid": v(3.26, -31.05) * mm, "end": v(3.52, -31.46) * mm});
            skLineSegment(sketch, "E89.3.79", {"start": v(-3.64, -70.73) * mm, "end": v(-8.46, -73.61) * mm});
            skArc(sketch, "E89.3.80", {"start": v(11.83, -56.56) * mm, "mid": v(11.37, -55.79) * mm, "end": v(10.8, -55.1) * mm});
            skArc(sketch, "E89.3.81", {"start": v(-3.18, -46.41) * mm, "mid": v(-3.26, -46.88) * mm, "end": v(-3.52, -47.28) * mm});
            skArc(sketch, "E89.3.82", {"start": v(3.17, -46.41) * mm, "mid": v(3.26, -46.88) * mm, "end": v(3.52, -47.28) * mm});
            skArc(sketch, "E89.3.83", {"start": v(-5.37, -39.03) * mm, "mid": v(-3.98, -38.72) * mm, "end": v(-3.17, -39.9) * mm});
            skArc(sketch, "E89.3.84", {"start": v(18.64, -48.04) * mm, "mid": v(18.18, -47.28) * mm, "end": v(17.62, -46.58) * mm});
            skArc(sketch, "E89.3.85", {"start": v(3.17, -64.65) * mm, "mid": v(3.26, -65.12) * mm, "end": v(3.52, -65.52) * mm});
            skArc(sketch, "E89.3.86", {"start": v(14.83, -49.18) * mm, "mid": v(15.49, -49.79) * mm, "end": v(16.22, -50.3) * mm});
            skLineSegment(sketch, "E89.3.87", {"start": v(-3.18, -46.41) * mm, "end": v(-3.18, -39.9) * mm});
            skLineSegment(sketch, "E89.3.88", {"start": v(9.4, -58.81) * mm, "end": v(14.52, -61.87) * mm});
            skArc(sketch, "E89.3.89", {"start": v(-3.18, -64.65) * mm, "mid": v(-3.26, -65.12) * mm, "end": v(-3.52, -65.52) * mm});
            skLineSegment(sketch, "E89.3.90", {"start": v(3.52, -65.52) * mm, "end": v(5.36, -67.5) * mm});
            skLineSegment(sketch, "E89.3.91", {"start": v(-3.52, -65.52) * mm, "end": v(-5.36, -67.5) * mm});
            skLineSegment(sketch, "E89.3.92", {"start": v(3.17, -75.95) * mm, "end": v(3.17, -71) * mm});
            skLineSegment(sketch, "E89.3.93", {"start": v(-3.18, -75.95) * mm, "end": v(-3.18, -71) * mm});
            skArc(sketch, "E89.3.94", {"start": v(-3.18, -75.95) * mm, "mid": v(-3.15, -76.2) * mm, "end": v(-3.08, -76.43) * mm});
            skArc(sketch, "E89.3.95", {"start": v(3.64, -70.73) * mm, "mid": v(3.33, -70.73) * mm, "end": v(3.17, -71) * mm});
            skArc(sketch, "E89.3.96", {"start": v(3.08, -76.43) * mm, "mid": v(3.15, -76.2) * mm, "end": v(3.17, -75.95) * mm});
            skArc(sketch, "E89.3.97", {"start": v(-3.64, -70.73) * mm, "mid": v(-3.33, -70.73) * mm, "end": v(-3.18, -71) * mm});
            skLineSegment(sketch, "E89.3.98", {"start": v(-3.18, -75.95) * mm, "end": v(-3.18, -71) * mm});
            skArc(sketch, "E89.3.99", {"start": v(-3.08, -76.43) * mm, "mid": v(-3.15, -76.2) * mm, "end": v(-3.18, -75.95) * mm});
            skPoint(sketch, "E89.4.0", {"position": v(35.44, -38.3) * mm});
            skPoint(sketch, "E89.4.1", {"position": v(61.34, -43.58) * mm});
            skPoint(sketch, "E89.4.2", {"position": v(28.51, -12.8) * mm});
            skPoint(sketch, "E89.4.3", {"position": v(68.4, -31.34) * mm});
            skLineSegment(sketch, "E89.4.4", {"start": v(67.73, -35.54) * mm, "end": v(72.8, -42.04) * mm});
            skLineSegment(sketch, "E89.4.5", {"start": v(72.8, -42.04) * mm, "end": v(64.65, -40.88) * mm});
            skLineSegment(sketch, "E89.4.6", {"start": v(27.76, -19.7) * mm, "end": v(35.54, -45.15) * mm});
            skPoint(sketch, "E89.4.7", {"position": v(39.04, -26.2) * mm});
            skPoint(sketch, "E89.4.8", {"position": v(59.43, -37.98) * mm});
            skPoint(sketch, "E89.4.9", {"position": v(54, -17.99) * mm});
            skPoint(sketch, "E89.4.10", {"position": v(67.55, -27.62) * mm});
            skPoint(sketch, "E89.4.11", {"position": v(54.84, -35.33) * mm});
            skLineSegment(sketch, "E89.4.12", {"start": v(29, -12.68) * mm, "end": v(49.15, -8.03) * mm});
            skPoint(sketch, "E89.4.13", {"position": v(44.5, -44.06) * mm});
            skPoint(sketch, "E89.4.14", {"position": v(46.22, -36.65) * mm});
            skPoint(sketch, "E89.4.15", {"position": v(30.18, -21.09) * mm});
            skLineSegment(sketch, "E89.4.16", {"start": v(25.48, -18.77) * mm, "end": v(31.53, -38.55) * mm});
            skPoint(sketch, "E89.4.17", {"position": v(37.36, -44.6) * mm});
            skPoint(sketch, "E89.4.18", {"position": v(57.3, -10.06) * mm});
            skPoint(sketch, "E89.4.19", {"position": v(42.21, -20.7) * mm});
            skPoint(sketch, "E89.4.20", {"position": v(25.34, -18.3) * mm});
            skLineSegment(sketch, "E89.4.21", {"start": v(39.18, -26.68) * mm, "end": v(42.3, -36.9) * mm});
            skPoint(sketch, "E89.4.22", {"position": v(33.72, -45.7) * mm});
            skPoint(sketch, "E89.4.23", {"position": v(48.14, -42.95) * mm});
            skPoint(sketch, "E89.4.24", {"position": v(43.88, -29) * mm});
            skPoint(sketch, "E89.4.25", {"position": v(60.4, -16.5) * mm});
            skLineSegment(sketch, "E89.4.26", {"start": v(54.4, -35.08) * mm, "end": v(46.67, -30.61) * mm});
            skPoint(sketch, "E89.4.27", {"position": v(56.44, -6.35) * mm});
            skLineSegment(sketch, "E89.4.28", {"start": v(35.17, -37.44) * mm, "end": v(31.12, -24.17) * mm});
            skPoint(sketch, "E89.4.29", {"position": v(42.57, -37.77) * mm});
            skPoint(sketch, "E89.4.30", {"position": v(31.8, -39.41) * mm});
            skPoint(sketch, "E89.4.31", {"position": v(57.7, -44.7) * mm});
            skLineSegment(sketch, "E89.4.32", {"start": v(50, -11.74) * mm, "end": v(36.5, -14.86) * mm});
            skLineSegment(sketch, "E89.4.33", {"start": v(30.93, -14.2) * mm, "end": v(56.87, -8.2) * mm});
            skPoint(sketch, "E89.4.34", {"position": v(58.01, -29.83) * mm});
            skLineSegment(sketch, "E89.4.35", {"start": v(42.7, -20.6) * mm, "end": v(53.12, -18.19) * mm});
            skPoint(sketch, "E89.4.36", {"position": v(67.58, -35.35) * mm});
            skPoint(sketch, "E89.4.37", {"position": v(50.03, -7.83) * mm});
            skPoint(sketch, "E89.4.38", {"position": v(62.6, -32.48) * mm});
            skLineSegment(sketch, "E89.4.39", {"start": v(57.58, -29.58) * mm, "end": v(49.84, -25.11) * mm});
            skPoint(sketch, "E89.4.40", {"position": v(50.88, -11.54) * mm});
            skPoint(sketch, "E89.4.41", {"position": v(33.35, -15.59) * mm});
            skPoint(sketch, "E89.4.42", {"position": v(54.85, -21.7) * mm});
            skPoint(sketch, "E89.4.43", {"position": v(64.4, -40.85) * mm});
            skPoint(sketch, "E89.4.44", {"position": v(61.27, -20.22) * mm});
            skPoint(sketch, "E89.4.45", {"position": v(47.05, -23.5) * mm});
            skLineSegment(sketch, "E89.4.46", {"start": v(54.84, -35.33) * mm, "end": v(46.67, -30.61) * mm});
            skLineSegment(sketch, "E89.4.47", {"start": v(44.63, -22.1) * mm, "end": v(60.84, -18.36) * mm});
            skLineSegment(sketch, "E89.4.48", {"start": v(28.08, -12.55) * mm, "end": v(23.41, -9.85) * mm});
            skPoint(sketch, "E89.4.49", {"position": v(64.4, -40.85) * mm});
            skLineSegment(sketch, "E89.4.50", {"start": v(25.34, -18.3) * mm, "end": v(20.24, -15.35) * mm});
            skLineSegment(sketch, "E89.4.52", {"start": v(41.46, -27.6) * mm, "end": v(46.32, -43.5) * mm});
            skLineSegment(sketch, "E89.4.53", {"start": v(55.77, -38.4) * mm, "end": v(59.52, -44.13) * mm});
            skLineSegment(sketch, "E89.4.54", {"start": v(39.04, -26.2) * mm, "end": v(32.97, -22.7) * mm});
            skArc(sketch, "E89.4.55", {"start": v(43.07, -38.52) * mm, "mid": v(42.63, -37.74) * mm, "end": v(42.3, -36.9) * mm});
            skLineSegment(sketch, "E89.4.56", {"start": v(41.78, -20.46) * mm, "end": v(36.14, -17.2) * mm});
            skLineSegment(sketch, "E89.4.57", {"start": v(43.07, -38.52) * mm, "end": v(46.32, -43.5) * mm});
            skLineSegment(sketch, "E89.4.58", {"start": v(61.14, -29.1) * mm, "end": v(67.98, -29.48) * mm});
            skLineSegment(sketch, "E89.4.59", {"start": v(54.9, -18.03) * mm, "end": v(60.84, -18.36) * mm});
            skLineSegment(sketch, "E89.4.60", {"start": v(32.29, -40.16) * mm, "end": v(35.54, -45.15) * mm});
            skArc(sketch, "E89.4.61", {"start": v(44.82, -32.08) * mm, "mid": v(45.24, -30.72) * mm, "end": v(46.67, -30.61) * mm});
            skLineSegment(sketch, "E89.4.62", {"start": v(45.95, -35.8) * mm, "end": v(44.82, -32.08) * mm});
            skArc(sketch, "E89.4.63", {"start": v(36.5, -14.86) * mm, "mid": v(35.52, -15.91) * mm, "end": v(36.14, -17.2) * mm});
            skLineSegment(sketch, "E89.4.64", {"start": v(35.45, -39.2) * mm, "end": v(35.54, -45.15) * mm});
            skArc(sketch, "E89.4.65", {"start": v(45.95, -35.8) * mm, "mid": v(46.15, -36.66) * mm, "end": v(46.23, -37.55) * mm});
            skArc(sketch, "E89.4.66", {"start": v(50.2, -22.77) * mm, "mid": v(49.22, -23.82) * mm, "end": v(49.84, -25.11) * mm});
            skArc(sketch, "E89.4.67", {"start": v(35.17, -37.44) * mm, "mid": v(35.37, -38.3) * mm, "end": v(35.45, -39.2) * mm});
            skLineSegment(sketch, "E89.4.68", {"start": v(46.23, -37.55) * mm, "end": v(46.32, -43.5) * mm});
            skArc(sketch, "E89.4.69", {"start": v(32.29, -40.16) * mm, "mid": v(31.85, -39.38) * mm, "end": v(31.53, -38.55) * mm});
            skArc(sketch, "E89.4.70", {"start": v(53.97, -21.9) * mm, "mid": v(54.83, -21.64) * mm, "end": v(55.64, -21.26) * mm});
            skLineSegment(sketch, "E89.4.71", {"start": v(63.07, -32.22) * mm, "end": v(67.98, -29.48) * mm});
            skLineSegment(sketch, "E89.4.72", {"start": v(60.43, -31.22) * mm, "end": v(67.98, -29.48) * mm});
            skLineSegment(sketch, "E89.4.73", {"start": v(50.93, -7.88) * mm, "end": v(56.87, -8.2) * mm});
            skLineSegment(sketch, "E89.4.74", {"start": v(57.26, -36.72) * mm, "end": v(59.52, -44.13) * mm});
            skArc(sketch, "E89.4.75", {"start": v(24.9, -18.04) * mm, "mid": v(25.26, -18.35) * mm, "end": v(25.48, -18.77) * mm});
            skLineSegment(sketch, "E89.4.76", {"start": v(53.97, -21.9) * mm, "end": v(50.2, -22.77) * mm});
            skLineSegment(sketch, "E89.4.77", {"start": v(51.67, -11.1) * mm, "end": v(56.87, -8.2) * mm});
            skArc(sketch, "E89.4.78", {"start": v(28.08, -12.55) * mm, "mid": v(28.53, -12.7) * mm, "end": v(29, -12.68) * mm});
            skLineSegment(sketch, "E89.4.79", {"start": v(59.44, -38.51) * mm, "end": v(59.52, -44.13) * mm});
            skArc(sketch, "E89.4.80", {"start": v(54.9, -18.03) * mm, "mid": v(54, -18.05) * mm, "end": v(53.12, -18.19) * mm});
            skArc(sketch, "E89.4.81", {"start": v(38.6, -25.95) * mm, "mid": v(38.96, -26.26) * mm, "end": v(39.18, -26.68) * mm});
            skArc(sketch, "E89.4.82", {"start": v(41.78, -20.46) * mm, "mid": v(42.23, -20.61) * mm, "end": v(42.7, -20.6) * mm});
            skArc(sketch, "E89.4.83", {"start": v(31.12, -24.17) * mm, "mid": v(31.54, -22.8) * mm, "end": v(32.97, -22.7) * mm});
            skArc(sketch, "E89.4.84", {"start": v(50.93, -7.88) * mm, "mid": v(50.03, -7.9) * mm, "end": v(49.15, -8.03) * mm});
            skArc(sketch, "E89.4.85", {"start": v(57.58, -29.58) * mm, "mid": v(58.03, -29.73) * mm, "end": v(58.5, -29.71) * mm});
            skArc(sketch, "E89.4.86", {"start": v(50, -11.74) * mm, "mid": v(50.86, -11.48) * mm, "end": v(51.67, -11.1) * mm});
            skLineSegment(sketch, "E89.4.87", {"start": v(38.6, -25.95) * mm, "end": v(32.97, -22.7) * mm});
            skLineSegment(sketch, "E89.4.88", {"start": v(55.64, -21.26) * mm, "end": v(60.84, -18.36) * mm});
            skArc(sketch, "E89.4.89", {"start": v(54.4, -35.08) * mm, "mid": v(54.76, -35.39) * mm, "end": v(54.98, -35.8) * mm});
            skLineSegment(sketch, "E89.4.90", {"start": v(58.5, -29.71) * mm, "end": v(61.14, -29.1) * mm});
            skLineSegment(sketch, "E89.4.91", {"start": v(54.98, -35.8) * mm, "end": v(55.77, -38.4) * mm});
            skLineSegment(sketch, "E89.4.92", {"start": v(67.37, -35.23) * mm, "end": v(63.07, -32.75) * mm});
            skLineSegment(sketch, "E89.4.93", {"start": v(64.2, -40.73) * mm, "end": v(59.9, -38.25) * mm});
            skArc(sketch, "E89.4.94", {"start": v(64.2, -40.73) * mm, "mid": v(64.41, -40.83) * mm, "end": v(64.65, -40.88) * mm});
            skArc(sketch, "E89.4.95", {"start": v(63.07, -32.22) * mm, "mid": v(62.92, -32.48) * mm, "end": v(63.07, -32.75) * mm});
            skArc(sketch, "E89.4.96", {"start": v(67.73, -35.54) * mm, "mid": v(67.56, -35.37) * mm, "end": v(67.37, -35.23) * mm});
            skArc(sketch, "E89.4.97", {"start": v(59.44, -38.51) * mm, "mid": v(59.59, -38.25) * mm, "end": v(59.9, -38.25) * mm});
            skLineSegment(sketch, "E89.4.98", {"start": v(64.2, -40.73) * mm, "end": v(59.9, -38.25) * mm});
            skArc(sketch, "E89.4.99", {"start": v(64.65, -40.88) * mm, "mid": v(64.41, -40.83) * mm, "end": v(64.2, -40.73) * mm});
            skPoint(sketch, "E89.5.0", {"position": v(50.88, 11.54) * mm});
            skPoint(sketch, "E89.5.1", {"position": v(68.4, 31.34) * mm});
            skPoint(sketch, "E89.5.2", {"position": v(25.34, 18.3) * mm});
            skPoint(sketch, "E89.5.3", {"position": v(61.34, 43.58) * mm});
            skLineSegment(sketch, "E89.5.4", {"start": v(64.65, 40.88) * mm, "end": v(72.8, 42.04) * mm});
            skLineSegment(sketch, "E89.5.5", {"start": v(72.8, 42.04) * mm, "end": v(67.73, 35.54) * mm});
            skLineSegment(sketch, "E89.5.6", {"start": v(30.93, 14.2) * mm, "end": v(56.87, 8.2) * mm});
            skPoint(sketch, "E89.5.7", {"position": v(42.21, 20.7) * mm});
            skPoint(sketch, "E89.5.8", {"position": v(62.6, 32.48) * mm});
            skPoint(sketch, "E89.5.9", {"position": v(42.57, 37.77) * mm});
            skPoint(sketch, "E89.5.10", {"position": v(57.7, 44.7) * mm});
            skPoint(sketch, "E89.5.11", {"position": v(58.01, 29.83) * mm});
            skLineSegment(sketch, "E89.5.12", {"start": v(25.48, 18.77) * mm, "end": v(31.53, 38.55) * mm});
            skPoint(sketch, "E89.5.13", {"position": v(60.4, 16.5) * mm});
            skPoint(sketch, "E89.5.14", {"position": v(54.85, 21.7) * mm});
            skPoint(sketch, "E89.5.15", {"position": v(33.35, 15.59) * mm});
            skLineSegment(sketch, "E89.5.16", {"start": v(29, 12.68) * mm, "end": v(49.15, 8.03) * mm});
            skPoint(sketch, "E89.5.17", {"position": v(57.3, 10.06) * mm});
            skPoint(sketch, "E89.5.18", {"position": v(37.36, 44.6) * mm});
            skPoint(sketch, "E89.5.19", {"position": v(39.04, 26.2) * mm});
            skPoint(sketch, "E89.5.20", {"position": v(28.51, 12.8) * mm});
            skLineSegment(sketch, "E89.5.21", {"start": v(42.7, 20.6) * mm, "end": v(53.12, 18.19) * mm});
            skPoint(sketch, "E89.5.22", {"position": v(56.44, 6.35) * mm});
            skPoint(sketch, "E89.5.23", {"position": v(61.27, 20.22) * mm});
            skPoint(sketch, "E89.5.24", {"position": v(47.05, 23.5) * mm});
            skPoint(sketch, "E89.5.25", {"position": v(44.5, 44.06) * mm});
            skLineSegment(sketch, "E89.5.26", {"start": v(57.58, 29.58) * mm, "end": v(49.84, 25.11) * mm});
            skPoint(sketch, "E89.5.27", {"position": v(33.72, 45.7) * mm});
            skLineSegment(sketch, "E89.5.28", {"start": v(50, 11.74) * mm, "end": v(36.5, 14.86) * mm});
            skPoint(sketch, "E89.5.29", {"position": v(54, 17.99) * mm});
            skPoint(sketch, "E89.5.30", {"position": v(50.03, 7.83) * mm});
            skPoint(sketch, "E89.5.31", {"position": v(67.55, 27.62) * mm});
            skLineSegment(sketch, "E89.5.32", {"start": v(35.17, 37.44) * mm, "end": v(31.12, 24.17) * mm});
            skLineSegment(sketch, "E89.5.33", {"start": v(27.76, 19.7) * mm, "end": v(35.54, 45.15) * mm});
            skPoint(sketch, "E89.5.34", {"position": v(54.84, 35.33) * mm});
            skLineSegment(sketch, "E89.5.35", {"start": v(39.18, 26.68) * mm, "end": v(42.3, 36.9) * mm});
            skPoint(sketch, "E89.5.36", {"position": v(64.4, 40.85) * mm});
            skPoint(sketch, "E89.5.37", {"position": v(31.8, 39.41) * mm});
            skPoint(sketch, "E89.5.38", {"position": v(59.43, 37.98) * mm});
            skLineSegment(sketch, "E89.5.39", {"start": v(54.4, 35.08) * mm, "end": v(46.67, 30.61) * mm});
            skPoint(sketch, "E89.5.40", {"position": v(35.44, 38.3) * mm});
            skPoint(sketch, "E89.5.41", {"position": v(30.18, 21.09) * mm});
            skPoint(sketch, "E89.5.42", {"position": v(46.22, 36.65) * mm});
            skPoint(sketch, "E89.5.43", {"position": v(67.58, 35.35) * mm});
            skPoint(sketch, "E89.5.44", {"position": v(48.14, 42.95) * mm});
            skPoint(sketch, "E89.5.45", {"position": v(43.88, 29) * mm});
            skLineSegment(sketch, "E89.5.46", {"start": v(58.01, 29.83) * mm, "end": v(49.84, 25.11) * mm});
            skLineSegment(sketch, "E89.5.47", {"start": v(41.46, 27.6) * mm, "end": v(46.32, 43.5) * mm});
            skLineSegment(sketch, "E89.5.48", {"start": v(24.9, 18.04) * mm, "end": v(20.24, 15.35) * mm});
            skPoint(sketch, "E89.5.49", {"position": v(67.58, 35.35) * mm});
            skLineSegment(sketch, "E89.5.50", {"start": v(28.51, 12.8) * mm, "end": v(23.41, 9.85) * mm});
            skLineSegment(sketch, "E89.5.52", {"start": v(44.63, 22.1) * mm, "end": v(60.84, 18.36) * mm});
            skLineSegment(sketch, "E89.5.53", {"start": v(61.14, 29.1) * mm, "end": v(67.98, 29.48) * mm});
            skLineSegment(sketch, "E89.5.54", {"start": v(42.21, 20.7) * mm, "end": v(36.14, 17.2) * mm});
            skArc(sketch, "E89.5.55", {"start": v(54.9, 18.03) * mm, "mid": v(54, 18.05) * mm, "end": v(53.12, 18.19) * mm});
            skLineSegment(sketch, "E89.5.56", {"start": v(38.6, 25.95) * mm, "end": v(32.97, 22.7) * mm});
            skLineSegment(sketch, "E89.5.57", {"start": v(54.9, 18.03) * mm, "end": v(60.84, 18.36) * mm});
            skLineSegment(sketch, "E89.5.58", {"start": v(55.77, 38.4) * mm, "end": v(59.52, 44.13) * mm});
            skLineSegment(sketch, "E89.5.59", {"start": v(43.07, 38.52) * mm, "end": v(46.32, 43.5) * mm});
            skLineSegment(sketch, "E89.5.60", {"start": v(50.93, 7.88) * mm, "end": v(56.87, 8.2) * mm});
            skArc(sketch, "E89.5.61", {"start": v(50.2, 22.77) * mm, "mid": v(49.22, 23.82) * mm, "end": v(49.84, 25.11) * mm});
            skLineSegment(sketch, "E89.5.62", {"start": v(53.97, 21.9) * mm, "end": v(50.2, 22.77) * mm});
            skArc(sketch, "E89.5.63", {"start": v(31.12, 24.17) * mm, "mid": v(31.54, 22.8) * mm, "end": v(32.97, 22.7) * mm});
            skLineSegment(sketch, "E89.5.64", {"start": v(51.67, 11.1) * mm, "end": v(56.87, 8.2) * mm});
            skArc(sketch, "E89.5.65", {"start": v(53.97, 21.9) * mm, "mid": v(54.83, 21.64) * mm, "end": v(55.64, 21.26) * mm});
            skArc(sketch, "E89.5.66", {"start": v(44.82, 32.08) * mm, "mid": v(45.24, 30.72) * mm, "end": v(46.67, 30.61) * mm});
            skArc(sketch, "E89.5.67", {"start": v(50, 11.74) * mm, "mid": v(50.86, 11.48) * mm, "end": v(51.67, 11.1) * mm});
            skLineSegment(sketch, "E89.5.68", {"start": v(55.64, 21.26) * mm, "end": v(60.84, 18.36) * mm});
            skArc(sketch, "E89.5.69", {"start": v(50.93, 7.88) * mm, "mid": v(50.03, 7.9) * mm, "end": v(49.15, 8.03) * mm});
            skArc(sketch, "E89.5.70", {"start": v(45.95, 35.8) * mm, "mid": v(46.15, 36.66) * mm, "end": v(46.23, 37.55) * mm});
            skLineSegment(sketch, "E89.5.71", {"start": v(59.44, 38.51) * mm, "end": v(59.52, 44.13) * mm});
            skLineSegment(sketch, "E89.5.72", {"start": v(57.26, 36.72) * mm, "end": v(59.52, 44.13) * mm});
            skLineSegment(sketch, "E89.5.73", {"start": v(32.29, 40.16) * mm, "end": v(35.54, 45.15) * mm});
            skLineSegment(sketch, "E89.5.74", {"start": v(60.43, 31.22) * mm, "end": v(67.98, 29.48) * mm});
            skArc(sketch, "E89.5.75", {"start": v(28.08, 12.55) * mm, "mid": v(28.53, 12.7) * mm, "end": v(29, 12.68) * mm});
            skLineSegment(sketch, "E89.5.76", {"start": v(45.95, 35.8) * mm, "end": v(44.82, 32.08) * mm});
            skLineSegment(sketch, "E89.5.77", {"start": v(35.45, 39.2) * mm, "end": v(35.54, 45.15) * mm});
            skArc(sketch, "E89.5.78", {"start": v(24.9, 18.04) * mm, "mid": v(25.26, 18.35) * mm, "end": v(25.48, 18.77) * mm});
            skLineSegment(sketch, "E89.5.79", {"start": v(63.07, 32.22) * mm, "end": v(67.98, 29.48) * mm});
            skArc(sketch, "E89.5.80", {"start": v(43.07, 38.52) * mm, "mid": v(42.63, 37.74) * mm, "end": v(42.3, 36.9) * mm});
            skArc(sketch, "E89.5.81", {"start": v(41.78, 20.46) * mm, "mid": v(42.23, 20.61) * mm, "end": v(42.7, 20.6) * mm});
            skArc(sketch, "E89.5.82", {"start": v(38.6, 25.95) * mm, "mid": v(38.96, 26.26) * mm, "end": v(39.18, 26.68) * mm});
            skArc(sketch, "E89.5.83", {"start": v(36.5, 14.86) * mm, "mid": v(35.52, 15.91) * mm, "end": v(36.14, 17.2) * mm});
            skArc(sketch, "E89.5.84", {"start": v(32.29, 40.16) * mm, "mid": v(31.85, 39.38) * mm, "end": v(31.53, 38.55) * mm});
            skArc(sketch, "E89.5.85", {"start": v(54.4, 35.08) * mm, "mid": v(54.76, 35.39) * mm, "end": v(54.98, 35.8) * mm});
            skArc(sketch, "E89.5.86", {"start": v(35.17, 37.44) * mm, "mid": v(35.37, 38.3) * mm, "end": v(35.45, 39.2) * mm});
            skLineSegment(sketch, "E89.5.87", {"start": v(41.78, 20.46) * mm, "end": v(36.14, 17.2) * mm});
            skLineSegment(sketch, "E89.5.88", {"start": v(46.23, 37.55) * mm, "end": v(46.32, 43.5) * mm});
            skArc(sketch, "E89.5.89", {"start": v(57.58, 29.58) * mm, "mid": v(58.03, 29.73) * mm, "end": v(58.5, 29.71) * mm});
            skLineSegment(sketch, "E89.5.90", {"start": v(54.98, 35.8) * mm, "end": v(55.77, 38.4) * mm});
            skLineSegment(sketch, "E89.5.91", {"start": v(58.5, 29.71) * mm, "end": v(61.14, 29.1) * mm});
            skLineSegment(sketch, "E89.5.92", {"start": v(64.2, 40.73) * mm, "end": v(59.9, 38.25) * mm});
            skLineSegment(sketch, "E89.5.93", {"start": v(67.37, 35.23) * mm, "end": v(63.07, 32.75) * mm});
            skArc(sketch, "E89.5.94", {"start": v(67.37, 35.23) * mm, "mid": v(67.56, 35.37) * mm, "end": v(67.73, 35.54) * mm});
            skArc(sketch, "E89.5.95", {"start": v(59.44, 38.51) * mm, "mid": v(59.59, 38.25) * mm, "end": v(59.9, 38.25) * mm});
            skArc(sketch, "E89.5.96", {"start": v(64.65, 40.88) * mm, "mid": v(64.41, 40.83) * mm, "end": v(64.2, 40.73) * mm});
            skArc(sketch, "E89.5.97", {"start": v(63.07, 32.22) * mm, "mid": v(62.92, 32.48) * mm, "end": v(63.07, 32.75) * mm});
            skLineSegment(sketch, "E89.5.98", {"start": v(67.37, 35.23) * mm, "end": v(63.07, 32.75) * mm});
            skArc(sketch, "E89.5.99", {"start": v(67.73, 35.54) * mm, "mid": v(67.56, 35.37) * mm, "end": v(67.37, 35.23) * mm});
            skArc(sketch, "E90.trimOffspring", {"start": v(-20.24, -15.35) * mm, "mid": v(-12.7, -22) * mm, "end": v(-3.18, -25.2) * mm});
            skArc(sketch, "E91.trimOffspring", {"start": v(3.17, -25.2) * mm, "mid": v(12.7, -22) * mm, "end": v(20.24, -15.35) * mm});
            skArc(sketch, "E92.trimOffspring", {"start": v(23.41, -9.85) * mm, "mid": v(25.4, 0) * mm, "end": v(23.41, 9.85) * mm});
            skArc(sketch, "E93.trimOffspring", {"start": v(20.24, 15.35) * mm, "mid": v(12.7, 22) * mm, "end": v(3.18, 25.2) * mm});
            skArc(sketch, "E94.trimOffspring", {"start": v(-3.17, 25.2) * mm, "mid": v(-12.7, 22) * mm, "end": v(-20.24, 15.35) * mm});
            skFitSpline(sketch, "E95", {"points": [v(0.73, 82.26) * mm, v(6.98, 88.4) * mm, v(14.16, 97.41) * mm, v(9.62, 105.54) * mm, v(0, 100.77) * mm], "startDerivative": vector(23.11, 25.34) * mm, "endDerivative": vector(-26.72, -37.63) * mm});
            skFitSpline(sketch, "E96.0", {"points": [v(-0.58, 83.46) * mm, v(-0.1, 84) * mm, v(0.9, 85.07) * mm, v(2.26, 86.44) * mm, v(3.42, 87.57) * mm, v(4.35, 88.43) * mm, v(5.33, 89.31) * mm, v(6.37, 90.22) * mm, v(7.44, 91.13) * mm, v(8.84, 92.35) * mm, v(10.12, 93.6) * mm, v(11.15, 94.87) * mm, v(11.76, 95.8) * mm, v(12.12, 96.58) * mm, v(12.3, 97.19) * mm, v(12.4, 97.64) * mm, v(12.45, 98.1) * mm, v(12.45, 98.77) * mm, v(12.35, 99.63) * mm, v(12.04, 100.66) * mm, v(11.58, 101.64) * mm, v(10.99, 102.5) * mm, v(10.43, 103.07) * mm, v(9.96, 103.43) * mm, v(9.6, 103.64) * mm, v(9.26, 103.8) * mm, v(8.91, 103.9) * mm, v(8.53, 103.96) * mm, v(8, 104) * mm, v(7.23, 103.9) * mm, v(6.23, 103.6) * mm, v(4.83, 102.95) * mm, v(3.09, 101.7) * mm, v(1.93, 100.4) * mm, v(1.45, 99.74) * mm]});
            skLineSegment(sketch, "E97", {"start": v(0, 84.07) * mm, "end": v(0, 114.62) * mm, "construction": true});
            skFitSpline(sketch, "E98.MirrorCS", {"points": [v(-0.73, 82.26) * mm, v(-6.98, 88.4) * mm, v(-14.16, 97.41) * mm, v(-9.62, 105.54) * mm, v(0, 100.77) * mm], "startDerivative": vector(-23.11, 25.34) * mm, "endDerivative": vector(26.72, -37.63) * mm});
            skFitSpline(sketch, "E99.0", {"points": [v(0.58, 83.46) * mm, v(0.1, 84) * mm, v(-0.9, 85.07) * mm, v(-2.26, 86.44) * mm, v(-3.42, 87.57) * mm, v(-4.35, 88.43) * mm, v(-5.33, 89.31) * mm, v(-6.37, 90.22) * mm, v(-7.44, 91.13) * mm, v(-8.84, 92.35) * mm, v(-10.12, 93.6) * mm, v(-11.15, 94.87) * mm, v(-11.76, 95.8) * mm, v(-12.12, 96.58) * mm, v(-12.3, 97.19) * mm, v(-12.4, 97.64) * mm, v(-12.45, 98.1) * mm, v(-12.45, 98.77) * mm, v(-12.35, 99.63) * mm, v(-12.04, 100.66) * mm, v(-11.58, 101.64) * mm, v(-10.99, 102.5) * mm, v(-10.43, 103.07) * mm, v(-9.96, 103.43) * mm, v(-9.6, 103.64) * mm, v(-9.26, 103.8) * mm, v(-8.91, 103.9) * mm, v(-8.53, 103.96) * mm, v(-8, 104) * mm, v(-7.23, 103.9) * mm, v(-6.23, 103.6) * mm, v(-4.83, 102.95) * mm, v(-3.09, 101.7) * mm, v(-1.93, 100.4) * mm, v(-1.45, 99.74) * mm]});
            skLineSegment(sketch, "E100", {"start": v(-1.43, 99.7) * mm, "end": v(0, 96.84) * mm});
            skLineSegment(sketch, "E101", {"start": v(0, 96.84) * mm, "end": v(1.43, 99.7) * mm});
            skPoint(sketch, "E102.visualSharp", {"position": v(-1.45, 99.74) * mm});
            skArc(sketch, "E102.filletArc", {"start": v(-1.43, 99.7) * mm, "mid": v(-1.45, 99.74) * mm, "end": v(-1.48, 99.78) * mm});
            skPoint(sketch, "E103.visualSharp", {"position": v(1.45, 99.74) * mm});
            skArc(sketch, "E103.filletArc", {"start": v(1.48, 99.78) * mm, "mid": v(1.45, 99.74) * mm, "end": v(1.43, 99.7) * mm});
            skSolve(sketch);
        }
        {
            var Q0;
            {var subQ6=sQuery(id+"F0.wireOp",EDGE,"E4.top");Q0=makeQuery(id+"F0.imprint","IMPRINT",FACE,{"disambiguationData":[TD([[makeQuery(id+"F0.imprint","IMPRINT",EDGE,{"derivedFrom":subQ6}),-1.0]])]});}
            var Q1;
            Q1=makeQuery(id+"F0.imprint","IMPRINT",FACE,{"disambiguationData":[TD([[makeQuery(id+"F0.imprint","IMPRINT",EDGE,{"derivedFrom":sQuery(id+"F0.wireOp",EDGE,"E89.4.4")}),-1.0]])]});
            var Q2;
            Q2=makeQuery(id+"F0.imprint","IMPRINT",FACE,{"disambiguationData":[TD([[makeQuery(id+"F0.imprint","IMPRINT",EDGE,{"derivedFrom":sQuery(id+"F0.wireOp",EDGE,"E89.3.4")}),-1.0]])]});
            var Q3;
            Q3=makeQuery(id+"F0.imprint","IMPRINT",FACE,{"disambiguationData":[TD([[makeQuery(id+"F0.imprint","IMPRINT",EDGE,{"derivedFrom":sQuery(id+"F0.wireOp",EDGE,"E89.2.4")}),-1.0]])]});
            var Q4;
            Q4=makeQuery(id+"F0.imprint","IMPRINT",FACE,{"disambiguationData":[TD([[makeQuery(id+"F0.imprint","IMPRINT",EDGE,{"derivedFrom":sQuery(id+"F0.wireOp",EDGE,"E89.1.4")}),-1.0]])]});
            var Q5;
            Q5=makeQuery(id+"F0.imprint","IMPRINT",FACE,{"disambiguationData":[TD([[makeQuery(id+"F0.imprint","IMPRINT",EDGE,{"derivedFrom":sQuery(id+"F0.wireOp",EDGE,"E4.left")}),1.0]])]});
            var Q6;
            Q6=makeQuery(id+"F0.imprint","IMPRINT",FACE,{"disambiguationData":[TD([[makeQuery(id+"F0.imprint","IMPRINT",EDGE,{"derivedFrom":sQuery(id+"F0.wireOp",EDGE,"E89.5.4")}),-1.0]])]});
            extrude(context, id + "F1", {"entities" : qUnion([Q0, Q1, Q2, Q3, Q4, Q5, Q6]), "depth" : 3.17 * mm, "offsetDistance" : 25.4 * mm});
        }
        {
            var Q0;
            Q0=makeQuery(id+"F1.opExtrude","CAP_FACE",FACE,{"disambiguationData":[OSD([sQuery(id+"F0.wireOp",EDGE,"E3"),sQuery(id+"F0.wireOp",EDGE,"E4.left"),sQuery(id+"F0.wireOp",EDGE,"E8"),sQuery(id+"F0.wireOp",EDGE,"E9"),sQuery(id+"F0.wireOp",EDGE,"E10"),sQuery(id+"F0.wireOp",EDGE,"E11"),sQuery(id+"F0.wireOp",EDGE,"E12"),sQuery(id+"F0.wireOp",EDGE,"E13"),sQuery(id+"F0.wireOp",EDGE,"E14"),sQuery(id+"F0.wireOp",EDGE,"E15"),sQuery(id+"F0.wireOp",EDGE,"E16"),sQuery(id+"F0.wireOp",EDGE,"E17"),sQuery(id+"F0.wireOp",EDGE,"E18"),sQuery(id+"F0.wireOp",EDGE,"E25.filletArc"),sQuery(id+"F0.wireOp",EDGE,"E26.filletArc"),sQuery(id+"F0.wireOp",EDGE,"E27.filletArc"),sQuery(id+"F0.wireOp",EDGE,"E28.filletArc"),sQuery(id+"F0.wireOp",EDGE,"E29.trimOffspring"),sQuery(id+"F0.wireOp",EDGE,"E30.trimOffspring"),sQuery(id+"F0.wireOp",EDGE,"E31.trimOffspring"),sQuery(id+"F0.wireOp",EDGE,"E32.filletArc"),sQuery(id+"F0.wireOp",EDGE,"E33.filletArc"),sQuery(id+"F0.wireOp",EDGE,"E34.filletArc"),sQuery(id+"F0.wireOp",EDGE,"E35.filletArc"),sQuery(id+"F0.wireOp",EDGE,"E36.filletArc"),sQuery(id+"F0.wireOp",EDGE,"E37.filletArc"),sQuery(id+"F0.wireOp",EDGE,"E38"),sQuery(id+"F0.wireOp",EDGE,"E39"),sQuery(id+"F0.wireOp",EDGE,"E40.filletArc"),sQuery(id+"F0.wireOp",EDGE,"E42.MirrorCS"),sQuery(id+"F0.wireOp",EDGE,"E43.MirrorCS"),sQuery(id+"F0.wireOp",EDGE,"E44.MirrorCS"),sQuery(id+"F0.wireOp",EDGE,"E45.MirrorCS"),sQuery(id+"F0.wireOp",EDGE,"E46.MirrorCS"),sQuery(id+"F0.wireOp",EDGE,"E47.MirrorCS"),sQuery(id+"F0.wireOp",EDGE,"E48.MirrorCS"),sQuery(id+"F0.wireOp",EDGE,"E49.MirrorCS"),sQuery(id+"F0.wireOp",EDGE,"E50.MirrorCS"),sQuery(id+"F0.wireOp",EDGE,"E51.MirrorCS"),sQuery(id+"F0.wireOp",EDGE,"E52.MirrorCS"),sQuery(id+"F0.wireOp",EDGE,"E53.MirrorCS"),sQuery(id+"F0.wireOp",EDGE,"E56.MirrorCS"),sQuery(id+"F0.wireOp",EDGE,"E57.MirrorCS"),sQuery(id+"F0.wireOp",EDGE,"E61.MirrorCS"),sQuery(id+"F0.wireOp",EDGE,"E62.MirrorCS"),sQuery(id+"F0.wireOp",EDGE,"E4.right"),sQuery(id+"F0.wireOp",EDGE,"E74.MirrorCS"),sQuery(id+"F0.wireOp",EDGE,"E76.MirrorCS"),sQuery(id+"F0.wireOp",EDGE,"E77.MirrorCS"),sQuery(id+"F0.wireOp",EDGE,"E80.MirrorCS"),sQuery(id+"F0.wireOp",EDGE,"E81.MirrorCS"),sQuery(id+"F0.wireOp",EDGE,"E82.MirrorCS"),sQuery(id+"F0.wireOp",EDGE,"E86.trimOffspring"),sQuery(id+"F0.wireOp",EDGE,"E87.trimOffspring"),sQuery(id+"F0.wireOp",EDGE,"E88.trimOffspring"),sQuery(id+"F0.wireOp",EDGE,"E89.1.4"),sQuery(id+"F0.wireOp",EDGE,"E89.1.5"),sQuery(id+"F0.wireOp",EDGE,"E89.1.12"),sQuery(id+"F0.wireOp",EDGE,"E89.1.16"),sQuery(id+"F0.wireOp",EDGE,"E89.1.21"),sQuery(id+"F0.wireOp",EDGE,"E89.1.28"),sQuery(id+"F0.wireOp",EDGE,"E89.1.32"),sQuery(id+"F0.wireOp",EDGE,"E89.1.35"),sQuery(id+"F0.wireOp",EDGE,"E89.1.39"),sQuery(id+"F0.wireOp",EDGE,"E89.1.46"),sQuery(id+"F0.wireOp",EDGE,"E89.1.48"),sQuery(id+"F0.wireOp",EDGE,"E89.1.50"),sQuery(id+"F0.wireOp",EDGE,"E89.1.53"),sQuery(id+"F0.wireOp",EDGE,"E89.1.55"),sQuery(id+"F0.wireOp",EDGE,"E89.1.56"),sQuery(id+"F0.wireOp",EDGE,"E89.1.57"),sQuery(id+"F0.wireOp",EDGE,"E89.1.58"),sQuery(id+"F0.wireOp",EDGE,"E89.1.59"),sQuery(id+"F0.wireOp",EDGE,"E89.1.60"),sQuery(id+"F0.wireOp",EDGE,"E89.1.61"),sQuery(id+"F0.wireOp",EDGE,"E89.1.62"),sQuery(id+"F0.wireOp",EDGE,"E89.1.63"),sQuery(id+"F0.wireOp",EDGE,"E89.1.64"),sQuery(id+"F0.wireOp",EDGE,"E89.1.65"),sQuery(id+"F0.wireOp",EDGE,"E89.1.66"),sQuery(id+"F0.wireOp",EDGE,"E89.1.67"),sQuery(id+"F0.wireOp",EDGE,"E89.1.68"),sQuery(id+"F0.wireOp",EDGE,"E89.1.69"),sQuery(id+"F0.wireOp",EDGE,"E89.1.70"),sQuery(id+"F0.wireOp",EDGE,"E89.1.71"),sQuery(id+"F0.wireOp",EDGE,"E89.1.73"),sQuery(id+"F0.wireOp",EDGE,"E89.1.75"),sQuery(id+"F0.wireOp",EDGE,"E89.1.76"),sQuery(id+"F0.wireOp",EDGE,"E89.1.77"),sQuery(id+"F0.wireOp",EDGE,"E89.1.78"),sQuery(id+"F0.wireOp",EDGE,"E89.1.79"),sQuery(id+"F0.wireOp",EDGE,"E89.1.80"),sQuery(id+"F0.wireOp",EDGE,"E89.1.81"),sQuery(id+"F0.wireOp",EDGE,"E89.1.82"),sQuery(id+"F0.wireOp",EDGE,"E89.1.83"),sQuery(id+"F0.wireOp",EDGE,"E89.1.84"),sQuery(id+"F0.wireOp",EDGE,"E89.1.85"),sQuery(id+"F0.wireOp",EDGE,"E89.1.86"),sQuery(id+"F0.wireOp",EDGE,"E89.1.87"),sQuery(id+"F0.wireOp",EDGE,"E89.1.88"),sQuery(id+"F0.wireOp",EDGE,"E89.1.89"),sQuery(id+"F0.wireOp",EDGE,"E89.1.90"),sQuery(id+"F0.wireOp",EDGE,"E89.1.91"),sQuery(id+"F0.wireOp",EDGE,"E89.1.92"),sQuery(id+"F0.wireOp",EDGE,"E89.1.95"),sQuery(id+"F0.wireOp",EDGE,"E89.1.96"),sQuery(id+"F0.wireOp",EDGE,"E89.1.97"),sQuery(id+"F0.wireOp",EDGE,"E89.1.98"),sQuery(id+"F0.wireOp",EDGE,"E89.1.99"),sQuery(id+"F0.wireOp",EDGE,"E89.2.4"),sQuery(id+"F0.wireOp",EDGE,"E89.2.5"),sQuery(id+"F0.wireOp",EDGE,"E89.2.12"),sQuery(id+"F0.wireOp",EDGE,"E89.2.16"),sQuery(id+"F0.wireOp",EDGE,"E89.2.21"),sQuery(id+"F0.wireOp",EDGE,"E89.2.28"),sQuery(id+"F0.wireOp",EDGE,"E89.2.32"),sQuery(id+"F0.wireOp",EDGE,"E89.2.35"),sQuery(id+"F0.wireOp",EDGE,"E89.2.39"),sQuery(id+"F0.wireOp",EDGE,"E89.2.46"),sQuery(id+"F0.wireOp",EDGE,"E89.2.48"),sQuery(id+"F0.wireOp",EDGE,"E89.2.50"),sQuery(id+"F0.wireOp",EDGE,"E89.2.53"),sQuery(id+"F0.wireOp",EDGE,"E89.2.55"),sQuery(id+"F0.wireOp",EDGE,"E89.2.56"),sQuery(id+"F0.wireOp",EDGE,"E89.2.57"),sQuery(id+"F0.wireOp",EDGE,"E89.2.58"),sQuery(id+"F0.wireOp",EDGE,"E89.2.59"),sQuery(id+"F0.wireOp",EDGE,"E89.2.60"),sQuery(id+"F0.wireOp",EDGE,"E89.2.61"),sQuery(id+"F0.wireOp",EDGE,"E89.2.62"),sQuery(id+"F0.wireOp",EDGE,"E89.2.63"),sQuery(id+"F0.wireOp",EDGE,"E89.2.64"),sQuery(id+"F0.wireOp",EDGE,"E89.2.65"),sQuery(id+"F0.wireOp",EDGE,"E89.2.66"),sQuery(id+"F0.wireOp",EDGE,"E89.2.67"),sQuery(id+"F0.wireOp",EDGE,"E89.2.68"),sQuery(id+"F0.wireOp",EDGE,"E89.2.69"),sQuery(id+"F0.wireOp",EDGE,"E89.2.70"),sQuery(id+"F0.wireOp",EDGE,"E89.2.71"),sQuery(id+"F0.wireOp",EDGE,"E89.2.73"),sQuery(id+"F0.wireOp",EDGE,"E89.2.75"),sQuery(id+"F0.wireOp",EDGE,"E89.2.76"),sQuery(id+"F0.wireOp",EDGE,"E89.2.77"),sQuery(id+"F0.wireOp",EDGE,"E89.2.78"),sQuery(id+"F0.wireOp",EDGE,"E89.2.79"),sQuery(id+"F0.wireOp",EDGE,"E89.2.80"),sQuery(id+"F0.wireOp",EDGE,"E89.2.81"),sQuery(id+"F0.wireOp",EDGE,"E89.2.82"),sQuery(id+"F0.wireOp",EDGE,"E89.2.83"),sQuery(id+"F0.wireOp",EDGE,"E89.2.84"),sQuery(id+"F0.wireOp",EDGE,"E89.2.85"),sQuery(id+"F0.wireOp",EDGE,"E89.2.86"),sQuery(id+"F0.wireOp",EDGE,"E89.2.87"),sQuery(id+"F0.wireOp",EDGE,"E89.2.88"),sQuery(id+"F0.wireOp",EDGE,"E89.2.89"),sQuery(id+"F0.wireOp",EDGE,"E89.2.90"),sQuery(id+"F0.wireOp",EDGE,"E89.2.91"),sQuery(id+"F0.wireOp",EDGE,"E89.2.92"),sQuery(id+"F0.wireOp",EDGE,"E89.2.95"),sQuery(id+"F0.wireOp",EDGE,"E89.2.96"),sQuery(id+"F0.wireOp",EDGE,"E89.2.97"),sQuery(id+"F0.wireOp",EDGE,"E89.2.98"),sQuery(id+"F0.wireOp",EDGE,"E89.2.99"),sQuery(id+"F0.wireOp",EDGE,"E89.3.4"),sQuery(id+"F0.wireOp",EDGE,"E89.3.5"),sQuery(id+"F0.wireOp",EDGE,"E89.3.12"),sQuery(id+"F0.wireOp",EDGE,"E89.3.16"),sQuery(id+"F0.wireOp",EDGE,"E89.3.21"),sQuery(id+"F0.wireOp",EDGE,"E89.3.28"),sQuery(id+"F0.wireOp",EDGE,"E89.3.32"),sQuery(id+"F0.wireOp",EDGE,"E89.3.35"),sQuery(id+"F0.wireOp",EDGE,"E89.3.39"),sQuery(id+"F0.wireOp",EDGE,"E89.3.46"),sQuery(id+"F0.wireOp",EDGE,"E89.3.48"),sQuery(id+"F0.wireOp",EDGE,"E89.3.50"),sQuery(id+"F0.wireOp",EDGE,"E89.3.53"),sQuery(id+"F0.wireOp",EDGE,"E89.3.55"),sQuery(id+"F0.wireOp",EDGE,"E89.3.56"),sQuery(id+"F0.wireOp",EDGE,"E89.3.57"),sQuery(id+"F0.wireOp",EDGE,"E89.3.58"),sQuery(id+"F0.wireOp",EDGE,"E89.3.59"),sQuery(id+"F0.wireOp",EDGE,"E89.3.60"),sQuery(id+"F0.wireOp",EDGE,"E89.3.61"),sQuery(id+"F0.wireOp",EDGE,"E89.3.62"),sQuery(id+"F0.wireOp",EDGE,"E89.3.63"),sQuery(id+"F0.wireOp",EDGE,"E89.3.64"),sQuery(id+"F0.wireOp",EDGE,"E89.3.65"),sQuery(id+"F0.wireOp",EDGE,"E89.3.66"),sQuery(id+"F0.wireOp",EDGE,"E89.3.67"),sQuery(id+"F0.wireOp",EDGE,"E89.3.68"),sQuery(id+"F0.wireOp",EDGE,"E89.3.69"),sQuery(id+"F0.wireOp",EDGE,"E89.3.70"),sQuery(id+"F0.wireOp",EDGE,"E89.3.71"),sQuery(id+"F0.wireOp",EDGE,"E89.3.73"),sQuery(id+"F0.wireOp",EDGE,"E89.3.75"),sQuery(id+"F0.wireOp",EDGE,"E89.3.76"),sQuery(id+"F0.wireOp",EDGE,"E89.3.77"),sQuery(id+"F0.wireOp",EDGE,"E89.3.78"),sQuery(id+"F0.wireOp",EDGE,"E89.3.79"),sQuery(id+"F0.wireOp",EDGE,"E89.3.80"),sQuery(id+"F0.wireOp",EDGE,"E89.3.81"),sQuery(id+"F0.wireOp",EDGE,"E89.3.82"),sQuery(id+"F0.wireOp",EDGE,"E89.3.83"),sQuery(id+"F0.wireOp",EDGE,"E89.3.84"),sQuery(id+"F0.wireOp",EDGE,"E89.3.85"),sQuery(id+"F0.wireOp",EDGE,"E89.3.86"),sQuery(id+"F0.wireOp",EDGE,"E89.3.87"),sQuery(id+"F0.wireOp",EDGE,"E89.3.88"),sQuery(id+"F0.wireOp",EDGE,"E89.3.89"),sQuery(id+"F0.wireOp",EDGE,"E89.3.90"),sQuery(id+"F0.wireOp",EDGE,"E89.3.91"),sQuery(id+"F0.wireOp",EDGE,"E89.3.92"),sQuery(id+"F0.wireOp",EDGE,"E89.3.95"),sQuery(id+"F0.wireOp",EDGE,"E89.3.96"),sQuery(id+"F0.wireOp",EDGE,"E89.3.97"),sQuery(id+"F0.wireOp",EDGE,"E89.3.98"),sQuery(id+"F0.wireOp",EDGE,"E89.3.99"),sQuery(id+"F0.wireOp",EDGE,"E89.4.4"),sQuery(id+"F0.wireOp",EDGE,"E89.4.5"),sQuery(id+"F0.wireOp",EDGE,"E89.4.12"),sQuery(id+"F0.wireOp",EDGE,"E89.4.16"),sQuery(id+"F0.wireOp",EDGE,"E89.4.21"),sQuery(id+"F0.wireOp",EDGE,"E89.4.28"),sQuery(id+"F0.wireOp",EDGE,"E89.4.32"),sQuery(id+"F0.wireOp",EDGE,"E89.4.35"),sQuery(id+"F0.wireOp",EDGE,"E89.4.39"),sQuery(id+"F0.wireOp",EDGE,"E89.4.46"),sQuery(id+"F0.wireOp",EDGE,"E89.4.48"),sQuery(id+"F0.wireOp",EDGE,"E89.4.50"),sQuery(id+"F0.wireOp",EDGE,"E89.4.53"),sQuery(id+"F0.wireOp",EDGE,"E89.4.55"),sQuery(id+"F0.wireOp",EDGE,"E89.4.56"),sQuery(id+"F0.wireOp",EDGE,"E89.4.57"),sQuery(id+"F0.wireOp",EDGE,"E89.4.58"),sQuery(id+"F0.wireOp",EDGE,"E89.4.59"),sQuery(id+"F0.wireOp",EDGE,"E89.4.60"),sQuery(id+"F0.wireOp",EDGE,"E89.4.61"),sQuery(id+"F0.wireOp",EDGE,"E89.4.62"),sQuery(id+"F0.wireOp",EDGE,"E89.4.63"),sQuery(id+"F0.wireOp",EDGE,"E89.4.64"),sQuery(id+"F0.wireOp",EDGE,"E89.4.65"),sQuery(id+"F0.wireOp",EDGE,"E89.4.66"),sQuery(id+"F0.wireOp",EDGE,"E89.4.67"),sQuery(id+"F0.wireOp",EDGE,"E89.4.68"),sQuery(id+"F0.wireOp",EDGE,"E89.4.69"),sQuery(id+"F0.wireOp",EDGE,"E89.4.70"),sQuery(id+"F0.wireOp",EDGE,"E89.4.71"),sQuery(id+"F0.wireOp",EDGE,"E89.4.73"),sQuery(id+"F0.wireOp",EDGE,"E89.4.75"),sQuery(id+"F0.wireOp",EDGE,"E89.4.76"),sQuery(id+"F0.wireOp",EDGE,"E89.4.77"),sQuery(id+"F0.wireOp",EDGE,"E89.4.78"),sQuery(id+"F0.wireOp",EDGE,"E89.4.79"),sQuery(id+"F0.wireOp",EDGE,"E89.4.80"),sQuery(id+"F0.wireOp",EDGE,"E89.4.81"),sQuery(id+"F0.wireOp",EDGE,"E89.4.82"),sQuery(id+"F0.wireOp",EDGE,"E89.4.83"),sQuery(id+"F0.wireOp",EDGE,"E89.4.84"),sQuery(id+"F0.wireOp",EDGE,"E89.4.85"),sQuery(id+"F0.wireOp",EDGE,"E89.4.86"),sQuery(id+"F0.wireOp",EDGE,"E89.4.87"),sQuery(id+"F0.wireOp",EDGE,"E89.4.88"),sQuery(id+"F0.wireOp",EDGE,"E89.4.89"),sQuery(id+"F0.wireOp",EDGE,"E89.4.90"),sQuery(id+"F0.wireOp",EDGE,"E89.4.91"),sQuery(id+"F0.wireOp",EDGE,"E89.4.92"),sQuery(id+"F0.wireOp",EDGE,"E89.4.95"),sQuery(id+"F0.wireOp",EDGE,"E89.4.96"),sQuery(id+"F0.wireOp",EDGE,"E89.4.97"),sQuery(id+"F0.wireOp",EDGE,"E89.4.98"),sQuery(id+"F0.wireOp",EDGE,"E89.4.99"),sQuery(id+"F0.wireOp",EDGE,"E89.5.4"),sQuery(id+"F0.wireOp",EDGE,"E89.5.5"),sQuery(id+"F0.wireOp",EDGE,"E89.5.12"),sQuery(id+"F0.wireOp",EDGE,"E89.5.16"),sQuery(id+"F0.wireOp",EDGE,"E89.5.21"),sQuery(id+"F0.wireOp",EDGE,"E89.5.28"),sQuery(id+"F0.wireOp",EDGE,"E89.5.32"),sQuery(id+"F0.wireOp",EDGE,"E89.5.35"),sQuery(id+"F0.wireOp",EDGE,"E89.5.39"),sQuery(id+"F0.wireOp",EDGE,"E89.5.46"),sQuery(id+"F0.wireOp",EDGE,"E89.5.48"),sQuery(id+"F0.wireOp",EDGE,"E89.5.50"),sQuery(id+"F0.wireOp",EDGE,"E89.5.53"),sQuery(id+"F0.wireOp",EDGE,"E89.5.55"),sQuery(id+"F0.wireOp",EDGE,"E89.5.56"),sQuery(id+"F0.wireOp",EDGE,"E89.5.57"),sQuery(id+"F0.wireOp",EDGE,"E89.5.58"),sQuery(id+"F0.wireOp",EDGE,"E89.5.59"),sQuery(id+"F0.wireOp",EDGE,"E89.5.60"),sQuery(id+"F0.wireOp",EDGE,"E89.5.61"),sQuery(id+"F0.wireOp",EDGE,"E89.5.62"),sQuery(id+"F0.wireOp",EDGE,"E89.5.63"),sQuery(id+"F0.wireOp",EDGE,"E89.5.64"),sQuery(id+"F0.wireOp",EDGE,"E89.5.65"),sQuery(id+"F0.wireOp",EDGE,"E89.5.66"),sQuery(id+"F0.wireOp",EDGE,"E89.5.67"),sQuery(id+"F0.wireOp",EDGE,"E89.5.68"),sQuery(id+"F0.wireOp",EDGE,"E89.5.69"),sQuery(id+"F0.wireOp",EDGE,"E89.5.70"),sQuery(id+"F0.wireOp",EDGE,"E89.5.71"),sQuery(id+"F0.wireOp",EDGE,"E89.5.73"),sQuery(id+"F0.wireOp",EDGE,"E89.5.75"),sQuery(id+"F0.wireOp",EDGE,"E89.5.76"),sQuery(id+"F0.wireOp",EDGE,"E89.5.77"),sQuery(id+"F0.wireOp",EDGE,"E89.5.78"),sQuery(id+"F0.wireOp",EDGE,"E89.5.79"),sQuery(id+"F0.wireOp",EDGE,"E89.5.80"),sQuery(id+"F0.wireOp",EDGE,"E89.5.81"),sQuery(id+"F0.wireOp",EDGE,"E89.5.82"),sQuery(id+"F0.wireOp",EDGE,"E89.5.83"),sQuery(id+"F0.wireOp",EDGE,"E89.5.84"),sQuery(id+"F0.wireOp",EDGE,"E89.5.85"),sQuery(id+"F0.wireOp",EDGE,"E89.5.86"),sQuery(id+"F0.wireOp",EDGE,"E89.5.87"),sQuery(id+"F0.wireOp",EDGE,"E89.5.88"),sQuery(id+"F0.wireOp",EDGE,"E89.5.89"),sQuery(id+"F0.wireOp",EDGE,"E89.5.90"),sQuery(id+"F0.wireOp",EDGE,"E89.5.91"),sQuery(id+"F0.wireOp",EDGE,"E89.5.92"),sQuery(id+"F0.wireOp",EDGE,"E89.5.95"),sQuery(id+"F0.wireOp",EDGE,"E89.5.96"),sQuery(id+"F0.wireOp",EDGE,"E89.5.97"),sQuery(id+"F0.wireOp",EDGE,"E89.5.98"),sQuery(id+"F0.wireOp",EDGE,"E89.5.99"),sQuery(id+"F0.wireOp",EDGE,"E90.trimOffspring"),sQuery(id+"F0.wireOp",EDGE,"E91.trimOffspring"),sQuery(id+"F0.wireOp",EDGE,"E92.trimOffspring"),sQuery(id+"F0.wireOp",EDGE,"E93.trimOffspring"),sQuery(id+"F0.wireOp",EDGE,"E94.trimOffspring")])],"isStart":false});
            var sketch = newSketch(context, id + "F2", { "sketchPlane" : qUnion([Q0])});
            skPoint(sketch, "E104.firstSnap0", {"position": v(-22.57, 16.7) * mm});
            skText(sketch, "E105", { "text": "Love You MORE\n  MOMMA!\n - Your Bama Boy", "fontName": "OpenSans-Italic.ttf"});
            const initialGuessF2  = {"E105": [-0.02185, 0.01043, 1, 0, 0.00422]};
            skSetInitialGuess(sketch, initialGuessF2);
            skSolve(sketch);
        }
        {
            var Q0;
            Q0 = qSketchRegion(id + "F2", true);
            extrude(context, id + "F3", {"entities" : qUnion([Q0]), "operationType" : NewBodyOperationType.ADD, "depth" : 1.27 * mm, "offsetDistance" : 25.4 * mm});
        }
        {
            var Q0;
            {var subQ3=sQuery(id+"F0.wireOp",EDGE,"E95");Q0=makeQuery(id+"F0.imprint","IMPRINT",FACE,{"disambiguationData":[TD([[makeQuery(id+"F0.imprint","IMPRINT",EDGE,{"derivedFrom":subQ3}),1.0]])]});}
            extrude(context, id + "F4", {"entities" : qUnion([Q0]), "operationType" : NewBodyOperationType.ADD, "depth" : 2.54 * mm, "offsetDistance" : 25.4 * mm});
        }
    });
